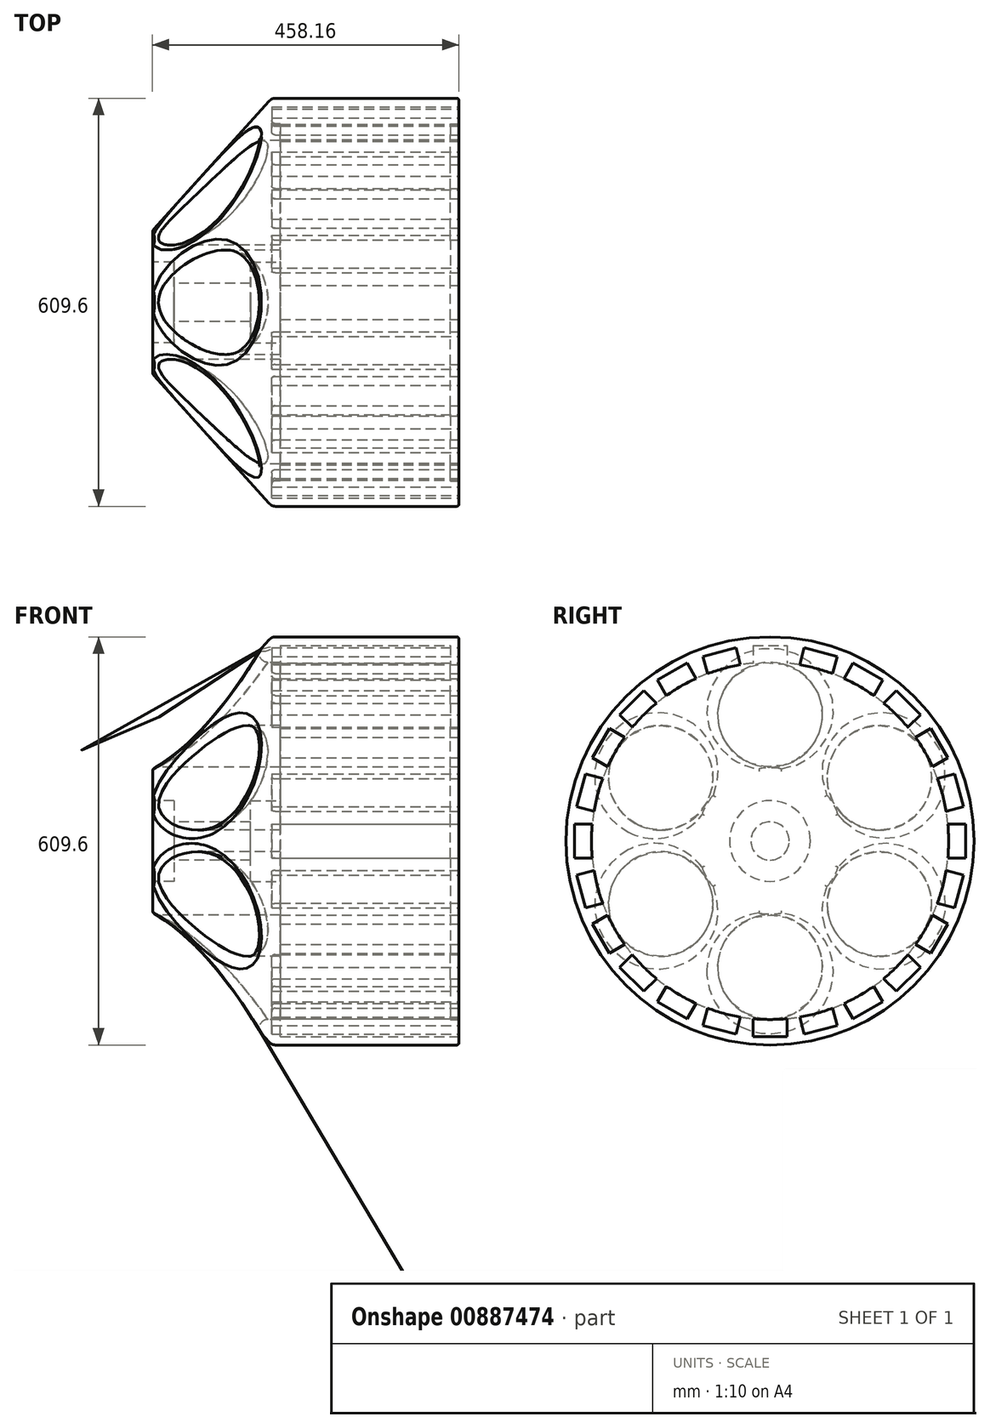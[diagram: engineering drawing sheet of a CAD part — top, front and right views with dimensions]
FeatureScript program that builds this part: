
annotation { "Feature Type Name" : "Feature", "Feature Type Description" : "" }
export const myFeature = defineFeature(function(context is Context, id is Id, definition is map)
    precondition{}
    {
        {
            var Q0;
            Q0=qCreatedBy(makeId("Front.planeOp"),FACE);
            var sketch = newSketch(context, id + "F0", { "sketchPlane" : qUnion([Q0])});
            skLineSegment(sketch, "E0", {"start": v(0, 0) * mm, "end": v(0, 304.8) * mm});
            skLineSegment(sketch, "E1", {"start": v(0, 304.8) * mm, "end": v(-279.4, 304.8) * mm});
            skLineSegment(sketch, "E2", {"start": v(-279.4, 304.8) * mm, "end": v(-457.2, 107.33) * mm});
            skLineSegment(sketch, "E3", {"start": v(-457.2, 107.33) * mm, "end": v(-457.2, 0) * mm});
            skArc(sketch, "E4", {"start": v(0, -309.7) * mm, "mid": v(-0.3, -303.83) * mm, "end": v(0, -297.95) * mm});
            skLineSegment(sketch, "E5", {"start": v(-457.2, 0) * mm, "end": v(0, 0) * mm});
            skSolve(sketch);
        }
        {
            var Q0;
            Q0=makeQuery(id+"F0.imprint","IMPRINT",FACE,{"disambiguationData":[TD([[makeQuery(id+"F0.imprint","IMPRINT",EDGE,{"derivedFrom":sQuery(id+"F0.wireOp",EDGE,"E0")}),1.0]])]});
            var Q1;
            Q1=sQuery(id+"F0.wireOp",EDGE,"E5");
            revolve(context, id + "F1", {"surfaceOperationType" : NewSurfaceOperationType.NEW, "entities" : qUnion([Q0]), "axis" : qUnion([Q1]), "revolveType" : RevolveType.FULL});
        }
        {
            var Q0;
            Q0=makeQuery(id+"F1.opRevolve","SWEPT_FACE",FACE,{"disambiguationData":[OSD([sQuery(id+"F0.wireOp",EDGE,"E0")])]});
            var sketch = newSketch(context, id + "F2", { "sketchPlane" : qUnion([Q0])});
            skCircle(sketch, "E6", {"center": v(0, 0) * mm, "radius": 266.7 * mm});
            skSolve(sketch);
        }
        {
            var Q0;
            Q0 = qSketchRegion(id + "F2", true);
            extrude(context, id + "F3", {"entities" : qUnion([Q0]), "operationType" : NewBodyOperationType.REMOVE, "oppositeDirection" : true, "depth" : 279.4 * mm, "offsetDistance" : 25.4 * mm});
        }
        {
            var Q0;
            Q0=makeQuery(id+"F1.opRevolve","SWEPT_FACE",FACE,{"disambiguationData":[OSD([sQuery(id+"F0.wireOp",EDGE,"E3")])]});
            var sketch = newSketch(context, id + "F4", { "sketchPlane" : qUnion([Q0])});
            skSolve(sketch);
        }
        {
            var Q0;
            Q0=makeQuery(id+"F4.imprint","IMPRINT",FACE,{"disambiguationData":[TD([[makeQuery(id+"F4.imprint","IMPRINT",EDGE,{"derivedFrom":makeQuery(id+"F1.opRevolve","SWEPT_EDGE",EDGE,{"disambiguationData":[OSD([sQuery(id+"F0.wireOp",EDGE,"E2"),sQuery(id+"F0.wireOp",EDGE,"E3")])]})}),1.0]])]});
            var sketch = newSketch(context, id + "F5", { "sketchPlane" : qUnion([Q0])});
            skSolve(sketch);
        }
        {
            var Q0;
            Q0=makeQuery(id+"F5.imprint","IMPRINT",FACE,{"disambiguationData":[TD([[makeQuery(id+"F5.imprint","IMPRINT",EDGE,{"derivedFrom":makeQuery(id+"F4.imprint","IMPRINT",EDGE,{"derivedFrom":makeQuery(id+"F1.opRevolve","SWEPT_EDGE",EDGE,{"disambiguationData":[OSD([sQuery(id+"F0.wireOp",EDGE,"E2"),sQuery(id+"F0.wireOp",EDGE,"E3")])]})})}),1.0]])]});
            var sketch = newSketch(context, id + "F6", { "sketchPlane" : qUnion([Q0])});
            skCircle(sketch, "E7", {"center": v(0, 0) * mm, "radius": 28.58 * mm});
            skSolve(sketch);
        }
        {
            var Q0;
            Q0 = qSketchRegion(id + "F6", true);
            extrude(context, id + "F7", {"entities" : qUnion([Q0]), "operationType" : NewBodyOperationType.REMOVE, "oppositeDirection" : true, "depth" : 298.68 * mm, "offsetDistance" : 25.4 * mm});
        }
        {
            var Q0;
            Q0=makeQuery(id+"F5.imprint","IMPRINT",FACE,{"disambiguationData":[TD([[makeQuery(id+"F5.imprint","IMPRINT",EDGE,{"derivedFrom":makeQuery(id+"F4.imprint","IMPRINT",EDGE,{"derivedFrom":makeQuery(id+"F1.opRevolve","SWEPT_EDGE",EDGE,{"disambiguationData":[OSD([sQuery(id+"F0.wireOp",EDGE,"E2"),sQuery(id+"F0.wireOp",EDGE,"E3")])]})})}),1.0]])]});
            var sketch = newSketch(context, id + "F8", { "sketchPlane" : qUnion([Q0])});
            skCircle(sketch, "E8", {"center": v(0, 0) * mm, "radius": 266.7 * mm, "construction": true});
            skCircle(sketch, "E9", {"center": v(0, 0) * mm, "radius": 101.6 * mm, "construction": true});
            skLineSegment(sketch, "E10.0", {"start": v(0, 266.7) * mm, "end": v(188.59, 188.59) * mm, "construction": true});
            skLineSegment(sketch, "E10.1", {"start": v(188.59, 188.59) * mm, "end": v(266.7, 0) * mm, "construction": true});
            skLineSegment(sketch, "E10.2", {"start": v(266.7, 0) * mm, "end": v(188.59, -188.59) * mm, "construction": true});
            skLineSegment(sketch, "E10.3", {"start": v(188.59, -188.59) * mm, "end": v(0, -266.7) * mm, "construction": true});
            skLineSegment(sketch, "E10.4", {"start": v(0, -266.7) * mm, "end": v(-188.59, -188.59) * mm, "construction": true});
            skLineSegment(sketch, "E10.5", {"start": v(-188.59, -188.59) * mm, "end": v(-266.7, 0) * mm, "construction": true});
            skLineSegment(sketch, "E10.6", {"start": v(-266.7, 0) * mm, "end": v(-188.59, 188.59) * mm, "construction": true});
            skLineSegment(sketch, "E10.7", {"start": v(-188.59, 188.59) * mm, "end": v(0, 266.7) * mm, "construction": true});
            skCircle(sketch, "E11", {"center": v(0, 188.59) * mm, "radius": 78.11 * mm});
            skCircle(sketch, "E12.1.0", {"center": v(-163.32, 94.3) * mm, "radius": 78.11 * mm});
            skCircle(sketch, "E12.2.0", {"center": v(-163.32, -94.3) * mm, "radius": 78.11 * mm});
            skCircle(sketch, "E12.3.0", {"center": v(0, -188.59) * mm, "radius": 78.11 * mm});
            skCircle(sketch, "E12.4.0", {"center": v(163.32, -94.3) * mm, "radius": 78.11 * mm});
            skCircle(sketch, "E12.5.0", {"center": v(163.32, 94.3) * mm, "radius": 78.11 * mm});
            skSolve(sketch);
        }
        {
            var Q0;
            Q0 = qSketchRegion(id + "F8", true);
            var sketch = newSketch(context, id + "F9", { "sketchPlane" : qUnion([Q0])});
            skSolve(sketch);
        }
        {
            var Q0;
            Q0 = qSketchRegion(id + "F8", true);
            var Q1;
            Q1=makeQuery(id+"F9.imprint","IMPRINT",FACE,{"disambiguationData":[TD([[makeQuery(id+"F9.imprint","IMPRINT",EDGE,{"derivedFrom":makeQuery(id+"F8.imprint","IMPRINT",EDGE,{"derivedFrom":sQuery(id+"F8.wireOp",EDGE,"E11")})}),1.0]])]});
            var Q2;
            Q2=makeQuery(id+"F9.imprint","IMPRINT",FACE,{"disambiguationData":[TD([[makeQuery(id+"F9.imprint","IMPRINT",EDGE,{"derivedFrom":makeQuery(id+"F8.imprint","IMPRINT",EDGE,{"derivedFrom":sQuery(id+"F8.wireOp",EDGE,"E12.4.0")})}),1.0]])]});
            var Q3;
            Q3=makeQuery(id+"F9.imprint","IMPRINT",FACE,{"disambiguationData":[TD([[makeQuery(id+"F9.imprint","IMPRINT",EDGE,{"derivedFrom":makeQuery(id+"F8.imprint","IMPRINT",EDGE,{"derivedFrom":sQuery(id+"F8.wireOp",EDGE,"E12.3.0")})}),1.0]])]});
            var Q4;
            Q4=makeQuery(id+"F9.imprint","IMPRINT",FACE,{"disambiguationData":[TD([[makeQuery(id+"F9.imprint","IMPRINT",EDGE,{"derivedFrom":makeQuery(id+"F8.imprint","IMPRINT",EDGE,{"derivedFrom":sQuery(id+"F8.wireOp",EDGE,"E12.2.0")})}),1.0]])]});
            var Q5;
            Q5=makeQuery(id+"F9.imprint","IMPRINT",FACE,{"disambiguationData":[TD([[makeQuery(id+"F9.imprint","IMPRINT",EDGE,{"derivedFrom":makeQuery(id+"F8.imprint","IMPRINT",EDGE,{"derivedFrom":sQuery(id+"F8.wireOp",EDGE,"E12.1.0")})}),1.0]])]});
            extrude(context, id + "F10", {"entities" : qUnion([Q0, Q1, Q2, Q3, Q4, Q5]), "operationType" : NewBodyOperationType.REMOVE, "oppositeDirection" : true, "depth" : 184.15 * mm, "offsetDistance" : 25.4 * mm});
        }
        {
            var Q0;
            Q0=makeQuery(id+"F5.imprint","IMPRINT",FACE,{"disambiguationData":[TD([[makeQuery(id+"F5.imprint","IMPRINT",EDGE,{"derivedFrom":makeQuery(id+"F4.imprint","IMPRINT",EDGE,{"derivedFrom":makeQuery(id+"F1.opRevolve","SWEPT_EDGE",EDGE,{"disambiguationData":[OSD([sQuery(id+"F0.wireOp",EDGE,"E2"),sQuery(id+"F0.wireOp",EDGE,"E3")])]})})}),1.0]])]});
            var sketch = newSketch(context, id + "F11", { "sketchPlane" : qUnion([Q0])});
            skCircle(sketch, "E13", {"center": v(0, 0) * mm, "radius": 60.33 * mm});
            skSolve(sketch);
        }
        {
            var Q0;
            Q0 = qSketchRegion(id + "F11", true);
            extrude(context, id + "F12", {"entities" : qUnion([Q0]), "operationType" : NewBodyOperationType.REMOVE, "oppositeDirection" : true, "depth" : 31.75 * mm, "offsetDistance" : 25.4 * mm});
        }
        {
            var Q0;
            Q0=makeQuery(id+"F3.boolean.opBoolean","COPY",FACE,{"derivedFrom":makeQuery(id+"F3.opExtrude","CAP_FACE",FACE,{"disambiguationData":[OSD([sQuery(id+"F2.wireOp",EDGE,"E6")])],"isStart":false})});
            var sketch = newSketch(context, id + "F13", { "sketchPlane" : qUnion([Q0])});
            skCircle(sketch, "E14", {"center": v(0, 0) * mm, "radius": 60.33 * mm});
            skSolve(sketch);
        }
        {
            var Q0;
            Q0 = qSketchRegion(id + "F13", true);
            var Q1;
            Q1=makeQuery(id+"F13.imprint","IMPRINT",FACE,{"disambiguationData":[TD([[makeQuery(id+"F13.imprint","IMPRINT",EDGE,{"derivedFrom":sQuery(id+"F13.wireOp",EDGE,"E14")}),1.0]])]});
            extrude(context, id + "F14", {"entities" : qUnion([Q0, Q1]), "operationType" : NewBodyOperationType.REMOVE, "oppositeDirection" : true, "depth" : 31.75 * mm, "offsetDistance" : 25.4 * mm});
        }
        {
            var Q0;
            Q0=makeQuery(id+"F1.opRevolve","SWEPT_FACE",FACE,{"disambiguationData":[OSD([sQuery(id+"F0.wireOp",EDGE,"E0")])]});
            var sketch = newSketch(context, id + "F15", { "sketchPlane" : qUnion([Q0])});
            skLineSegment(sketch, "E15", {"start": v(0, 292.1) * mm, "end": v(0, 266.7) * mm, "construction": true});
            skLineSegment(sketch, "E16", {"start": v(0, 292.1) * mm, "end": v(25.4, 292.1) * mm});
            skLineSegment(sketch, "E17", {"start": v(25.4, 292.1) * mm, "end": v(25.4, 265.49) * mm});
            skLineSegment(sketch, "E18.MirrorCS", {"start": v(0, 292.1) * mm, "end": v(-25.4, 292.1) * mm});
            skLineSegment(sketch, "E19.MirrorCS", {"start": v(-25.4, 292.1) * mm, "end": v(-25.4, 265.49) * mm});
            skLineSegment(sketch, "E20.1.0", {"start": v(-51.07, 288.72) * mm, "end": v(-44.18, 263.02) * mm});
            skLineSegment(sketch, "E20.1.1", {"start": v(-75.6, 282.15) * mm, "end": v(-51.07, 288.72) * mm});
            skLineSegment(sketch, "E20.1.2", {"start": v(-75.6, 282.15) * mm, "end": v(-100.14, 275.57) * mm});
            skLineSegment(sketch, "E20.1.3", {"start": v(-100.14, 275.57) * mm, "end": v(-93.25, 249.87) * mm});
            skLineSegment(sketch, "E20.2.0", {"start": v(-124.05, 265.67) * mm, "end": v(-110.75, 242.62) * mm});
            skLineSegment(sketch, "E20.2.1", {"start": v(-146.05, 252.97) * mm, "end": v(-124.05, 265.67) * mm});
            skLineSegment(sketch, "E20.2.2", {"start": v(-146.05, 252.97) * mm, "end": v(-168.05, 240.27) * mm});
            skLineSegment(sketch, "E20.2.3", {"start": v(-168.05, 240.27) * mm, "end": v(-154.74, 217.22) * mm});
            skLineSegment(sketch, "E20.3.0", {"start": v(-188.59, 224.5) * mm, "end": v(-169.77, 205.69) * mm});
            skLineSegment(sketch, "E20.3.1", {"start": v(-206.55, 206.55) * mm, "end": v(-188.59, 224.5) * mm});
            skLineSegment(sketch, "E20.3.2", {"start": v(-206.55, 206.55) * mm, "end": v(-224.5, 188.59) * mm});
            skLineSegment(sketch, "E20.3.3", {"start": v(-224.5, 188.59) * mm, "end": v(-205.69, 169.77) * mm});
            skLineSegment(sketch, "E20.4.0", {"start": v(-240.27, 168.05) * mm, "end": v(-217.22, 154.74) * mm});
            skLineSegment(sketch, "E20.4.1", {"start": v(-252.97, 146.05) * mm, "end": v(-240.27, 168.05) * mm});
            skLineSegment(sketch, "E20.4.2", {"start": v(-252.97, 146.05) * mm, "end": v(-265.67, 124.05) * mm});
            skLineSegment(sketch, "E20.4.3", {"start": v(-265.67, 124.05) * mm, "end": v(-242.62, 110.75) * mm});
            skLineSegment(sketch, "E20.5.0", {"start": v(-275.57, 100.14) * mm, "end": v(-249.87, 93.25) * mm});
            skLineSegment(sketch, "E20.5.1", {"start": v(-282.15, 75.6) * mm, "end": v(-275.57, 100.14) * mm});
            skLineSegment(sketch, "E20.5.2", {"start": v(-282.15, 75.6) * mm, "end": v(-288.72, 51.07) * mm});
            skLineSegment(sketch, "E20.5.3", {"start": v(-288.72, 51.07) * mm, "end": v(-263.02, 44.18) * mm});
            skLineSegment(sketch, "E20.6.0", {"start": v(-292.1, 25.4) * mm, "end": v(-265.49, 25.4) * mm});
            skLineSegment(sketch, "E20.6.1", {"start": v(-292.1, 0) * mm, "end": v(-292.1, 25.4) * mm});
            skLineSegment(sketch, "E20.6.2", {"start": v(-292.1, 0) * mm, "end": v(-292.1, -25.4) * mm});
            skLineSegment(sketch, "E20.6.3", {"start": v(-292.1, -25.4) * mm, "end": v(-265.49, -25.4) * mm});
            skLineSegment(sketch, "E20.7.0", {"start": v(-288.72, -51.07) * mm, "end": v(-263.02, -44.18) * mm});
            skLineSegment(sketch, "E20.7.1", {"start": v(-282.15, -75.6) * mm, "end": v(-288.72, -51.07) * mm});
            skLineSegment(sketch, "E20.7.2", {"start": v(-282.15, -75.6) * mm, "end": v(-275.57, -100.14) * mm});
            skLineSegment(sketch, "E20.7.3", {"start": v(-275.57, -100.14) * mm, "end": v(-249.87, -93.25) * mm});
            skLineSegment(sketch, "E20.8.0", {"start": v(-265.67, -124.05) * mm, "end": v(-242.62, -110.75) * mm});
            skLineSegment(sketch, "E20.8.1", {"start": v(-252.97, -146.05) * mm, "end": v(-265.67, -124.05) * mm});
            skLineSegment(sketch, "E20.8.2", {"start": v(-252.97, -146.05) * mm, "end": v(-240.27, -168.05) * mm});
            skLineSegment(sketch, "E20.8.3", {"start": v(-240.27, -168.05) * mm, "end": v(-217.22, -154.74) * mm});
            skLineSegment(sketch, "E20.9.0", {"start": v(-224.5, -188.59) * mm, "end": v(-205.69, -169.77) * mm});
            skLineSegment(sketch, "E20.9.1", {"start": v(-206.55, -206.55) * mm, "end": v(-224.5, -188.59) * mm});
            skLineSegment(sketch, "E20.9.2", {"start": v(-206.55, -206.55) * mm, "end": v(-188.59, -224.5) * mm});
            skLineSegment(sketch, "E20.9.3", {"start": v(-188.59, -224.5) * mm, "end": v(-169.77, -205.69) * mm});
            skLineSegment(sketch, "E20.10.0", {"start": v(-168.05, -240.27) * mm, "end": v(-154.74, -217.22) * mm});
            skLineSegment(sketch, "E20.10.1", {"start": v(-146.05, -252.97) * mm, "end": v(-168.05, -240.27) * mm});
            skLineSegment(sketch, "E20.10.2", {"start": v(-146.05, -252.97) * mm, "end": v(-124.05, -265.67) * mm});
            skLineSegment(sketch, "E20.10.3", {"start": v(-124.05, -265.67) * mm, "end": v(-110.75, -242.62) * mm});
            skLineSegment(sketch, "E20.11.0", {"start": v(-100.14, -275.57) * mm, "end": v(-93.25, -249.87) * mm});
            skLineSegment(sketch, "E20.11.1", {"start": v(-75.6, -282.15) * mm, "end": v(-100.14, -275.57) * mm});
            skLineSegment(sketch, "E20.11.2", {"start": v(-75.6, -282.15) * mm, "end": v(-51.07, -288.72) * mm});
            skLineSegment(sketch, "E20.11.3", {"start": v(-51.07, -288.72) * mm, "end": v(-44.18, -263.02) * mm});
            skLineSegment(sketch, "E20.12.0", {"start": v(-25.4, -292.1) * mm, "end": v(-25.4, -265.49) * mm});
            skLineSegment(sketch, "E20.12.1", {"start": v(0, -292.1) * mm, "end": v(-25.4, -292.1) * mm});
            skLineSegment(sketch, "E20.12.2", {"start": v(0, -292.1) * mm, "end": v(25.4, -292.1) * mm});
            skLineSegment(sketch, "E20.12.3", {"start": v(25.4, -292.1) * mm, "end": v(25.4, -265.49) * mm});
            skLineSegment(sketch, "E20.13.0", {"start": v(51.07, -288.72) * mm, "end": v(44.18, -263.02) * mm});
            skLineSegment(sketch, "E20.13.1", {"start": v(75.6, -282.15) * mm, "end": v(51.07, -288.72) * mm});
            skLineSegment(sketch, "E20.13.2", {"start": v(75.6, -282.15) * mm, "end": v(100.14, -275.57) * mm});
            skLineSegment(sketch, "E20.13.3", {"start": v(100.14, -275.57) * mm, "end": v(93.25, -249.87) * mm});
            skLineSegment(sketch, "E20.14.0", {"start": v(124.05, -265.67) * mm, "end": v(110.75, -242.62) * mm});
            skLineSegment(sketch, "E20.14.1", {"start": v(146.05, -252.97) * mm, "end": v(124.05, -265.67) * mm});
            skLineSegment(sketch, "E20.14.2", {"start": v(146.05, -252.97) * mm, "end": v(168.05, -240.27) * mm});
            skLineSegment(sketch, "E20.14.3", {"start": v(168.05, -240.27) * mm, "end": v(154.74, -217.22) * mm});
            skLineSegment(sketch, "E20.15.0", {"start": v(188.59, -224.5) * mm, "end": v(169.77, -205.69) * mm});
            skLineSegment(sketch, "E20.15.1", {"start": v(206.55, -206.55) * mm, "end": v(188.59, -224.5) * mm});
            skLineSegment(sketch, "E20.15.2", {"start": v(206.55, -206.55) * mm, "end": v(224.5, -188.59) * mm});
            skLineSegment(sketch, "E20.15.3", {"start": v(224.5, -188.59) * mm, "end": v(205.69, -169.77) * mm});
            skLineSegment(sketch, "E20.16.0", {"start": v(240.27, -168.05) * mm, "end": v(217.22, -154.74) * mm});
            skLineSegment(sketch, "E20.16.1", {"start": v(252.97, -146.05) * mm, "end": v(240.27, -168.05) * mm});
            skLineSegment(sketch, "E20.16.2", {"start": v(252.97, -146.05) * mm, "end": v(265.67, -124.05) * mm});
            skLineSegment(sketch, "E20.16.3", {"start": v(265.67, -124.05) * mm, "end": v(242.62, -110.75) * mm});
            skLineSegment(sketch, "E20.17.0", {"start": v(275.57, -100.14) * mm, "end": v(249.87, -93.25) * mm});
            skLineSegment(sketch, "E20.17.1", {"start": v(282.15, -75.6) * mm, "end": v(275.57, -100.14) * mm});
            skLineSegment(sketch, "E20.17.2", {"start": v(282.15, -75.6) * mm, "end": v(288.72, -51.07) * mm});
            skLineSegment(sketch, "E20.17.3", {"start": v(288.72, -51.07) * mm, "end": v(263.02, -44.18) * mm});
            skLineSegment(sketch, "E20.18.0", {"start": v(292.1, -25.4) * mm, "end": v(265.49, -25.4) * mm});
            skLineSegment(sketch, "E20.18.1", {"start": v(292.1, 0) * mm, "end": v(292.1, -25.4) * mm});
            skLineSegment(sketch, "E20.18.2", {"start": v(292.1, 0) * mm, "end": v(292.1, 25.4) * mm});
            skLineSegment(sketch, "E20.18.3", {"start": v(292.1, 25.4) * mm, "end": v(265.49, 25.4) * mm});
            skLineSegment(sketch, "E20.19.0", {"start": v(288.72, 51.07) * mm, "end": v(263.02, 44.18) * mm});
            skLineSegment(sketch, "E20.19.1", {"start": v(282.15, 75.6) * mm, "end": v(288.72, 51.07) * mm});
            skLineSegment(sketch, "E20.19.2", {"start": v(282.15, 75.6) * mm, "end": v(275.57, 100.14) * mm});
            skLineSegment(sketch, "E20.19.3", {"start": v(275.57, 100.14) * mm, "end": v(249.87, 93.25) * mm});
            skLineSegment(sketch, "E20.20.0", {"start": v(265.67, 124.05) * mm, "end": v(242.62, 110.75) * mm});
            skLineSegment(sketch, "E20.20.1", {"start": v(252.97, 146.05) * mm, "end": v(265.67, 124.05) * mm});
            skLineSegment(sketch, "E20.20.2", {"start": v(252.97, 146.05) * mm, "end": v(240.27, 168.05) * mm});
            skLineSegment(sketch, "E20.20.3", {"start": v(240.27, 168.05) * mm, "end": v(217.22, 154.74) * mm});
            skLineSegment(sketch, "E20.21.0", {"start": v(224.5, 188.59) * mm, "end": v(205.69, 169.77) * mm});
            skLineSegment(sketch, "E20.21.1", {"start": v(206.55, 206.55) * mm, "end": v(224.5, 188.59) * mm});
            skLineSegment(sketch, "E20.21.2", {"start": v(206.55, 206.55) * mm, "end": v(188.59, 224.5) * mm});
            skLineSegment(sketch, "E20.21.3", {"start": v(188.59, 224.5) * mm, "end": v(169.77, 205.69) * mm});
            skLineSegment(sketch, "E20.22.0", {"start": v(168.05, 240.27) * mm, "end": v(154.74, 217.22) * mm});
            skLineSegment(sketch, "E20.22.1", {"start": v(146.05, 252.97) * mm, "end": v(168.05, 240.27) * mm});
            skLineSegment(sketch, "E20.22.2", {"start": v(146.05, 252.97) * mm, "end": v(124.05, 265.67) * mm});
            skLineSegment(sketch, "E20.22.3", {"start": v(124.05, 265.67) * mm, "end": v(110.75, 242.62) * mm});
            skLineSegment(sketch, "E20.23.0", {"start": v(100.14, 275.57) * mm, "end": v(93.25, 249.87) * mm});
            skLineSegment(sketch, "E20.23.1", {"start": v(75.6, 282.15) * mm, "end": v(100.14, 275.57) * mm});
            skLineSegment(sketch, "E20.23.2", {"start": v(75.6, 282.15) * mm, "end": v(51.07, 288.72) * mm});
            skLineSegment(sketch, "E20.23.3", {"start": v(51.07, 288.72) * mm, "end": v(44.18, 263.02) * mm});
            skPoint(sketch, "E20.center", {"position": v(0, 0) * mm});
            skSolve(sketch);
        }
        {
            var Q0;
            Q0=makeQuery(id+"F15.imprint","IMPRINT",FACE,{"disambiguationData":[TD([[makeQuery(id+"F15.imprint","IMPRINT",EDGE,{"derivedFrom":sQuery(id+"F15.wireOp",EDGE,"E16")}),-1.0]])]});
            var Q1;
            {var subQ1=sQuery(id+"F15.wireOp",EDGE,"E20.23.0");Q1=makeQuery(id+"F15.imprint","IMPRINT",FACE,{"disambiguationData":[TD([[makeQuery(id+"F15.imprint","IMPRINT",EDGE,{"derivedFrom":subQ1}),-1.0]])]});}
            var Q2;
            {var subQ1=sQuery(id+"F15.wireOp",EDGE,"E20.22.0");Q2=makeQuery(id+"F15.imprint","IMPRINT",FACE,{"disambiguationData":[TD([[makeQuery(id+"F15.imprint","IMPRINT",EDGE,{"derivedFrom":subQ1}),-1.0]])]});}
            var Q3;
            {var subQ1=sQuery(id+"F15.wireOp",EDGE,"E20.21.0");Q3=makeQuery(id+"F15.imprint","IMPRINT",FACE,{"disambiguationData":[TD([[makeQuery(id+"F15.imprint","IMPRINT",EDGE,{"derivedFrom":subQ1}),-1.0]])]});}
            var Q4;
            {var subQ1=sQuery(id+"F15.wireOp",EDGE,"E20.20.0");Q4=makeQuery(id+"F15.imprint","IMPRINT",FACE,{"disambiguationData":[TD([[makeQuery(id+"F15.imprint","IMPRINT",EDGE,{"derivedFrom":subQ1}),-1.0]])]});}
            var Q5;
            {var subQ1=sQuery(id+"F15.wireOp",EDGE,"E20.19.0");Q5=makeQuery(id+"F15.imprint","IMPRINT",FACE,{"disambiguationData":[TD([[makeQuery(id+"F15.imprint","IMPRINT",EDGE,{"derivedFrom":subQ1}),-1.0]])]});}
            var Q6;
            {var subQ1=sQuery(id+"F15.wireOp",EDGE,"E20.17.0");Q6=makeQuery(id+"F15.imprint","IMPRINT",FACE,{"disambiguationData":[TD([[makeQuery(id+"F15.imprint","IMPRINT",EDGE,{"derivedFrom":subQ1}),-1.0]])]});}
            var Q7;
            {var subQ1=sQuery(id+"F15.wireOp",EDGE,"E20.16.0");Q7=makeQuery(id+"F15.imprint","IMPRINT",FACE,{"disambiguationData":[TD([[makeQuery(id+"F15.imprint","IMPRINT",EDGE,{"derivedFrom":subQ1}),-1.0]])]});}
            var Q8;
            {var subQ1=sQuery(id+"F15.wireOp",EDGE,"E20.15.0");Q8=makeQuery(id+"F15.imprint","IMPRINT",FACE,{"disambiguationData":[TD([[makeQuery(id+"F15.imprint","IMPRINT",EDGE,{"derivedFrom":subQ1}),-1.0]])]});}
            var Q9;
            {var subQ1=sQuery(id+"F15.wireOp",EDGE,"E20.14.0");Q9=makeQuery(id+"F15.imprint","IMPRINT",FACE,{"disambiguationData":[TD([[makeQuery(id+"F15.imprint","IMPRINT",EDGE,{"derivedFrom":subQ1}),-1.0]])]});}
            var Q10;
            {var subQ1=sQuery(id+"F15.wireOp",EDGE,"E20.13.0");Q10=makeQuery(id+"F15.imprint","IMPRINT",FACE,{"disambiguationData":[TD([[makeQuery(id+"F15.imprint","IMPRINT",EDGE,{"derivedFrom":subQ1}),-1.0]])]});}
            var Q11;
            {var subQ1=sQuery(id+"F15.wireOp",EDGE,"E20.12.0");Q11=makeQuery(id+"F15.imprint","IMPRINT",FACE,{"disambiguationData":[TD([[makeQuery(id+"F15.imprint","IMPRINT",EDGE,{"derivedFrom":subQ1}),-1.0]])]});}
            var Q12;
            {var subQ1=sQuery(id+"F15.wireOp",EDGE,"E20.11.0");Q12=makeQuery(id+"F15.imprint","IMPRINT",FACE,{"disambiguationData":[TD([[makeQuery(id+"F15.imprint","IMPRINT",EDGE,{"derivedFrom":subQ1}),-1.0]])]});}
            var Q13;
            {var subQ1=sQuery(id+"F15.wireOp",EDGE,"E20.10.0");Q13=makeQuery(id+"F15.imprint","IMPRINT",FACE,{"disambiguationData":[TD([[makeQuery(id+"F15.imprint","IMPRINT",EDGE,{"derivedFrom":subQ1}),-1.0]])]});}
            var Q14;
            {var subQ1=sQuery(id+"F15.wireOp",EDGE,"E20.8.0");Q14=makeQuery(id+"F15.imprint","IMPRINT",FACE,{"disambiguationData":[TD([[makeQuery(id+"F15.imprint","IMPRINT",EDGE,{"derivedFrom":subQ1}),-1.0]])]});}
            var Q15;
            {var subQ1=sQuery(id+"F15.wireOp",EDGE,"E20.7.0");Q15=makeQuery(id+"F15.imprint","IMPRINT",FACE,{"disambiguationData":[TD([[makeQuery(id+"F15.imprint","IMPRINT",EDGE,{"derivedFrom":subQ1}),-1.0]])]});}
            var Q16;
            {var subQ1=sQuery(id+"F15.wireOp",EDGE,"E20.9.0");Q16=makeQuery(id+"F15.imprint","IMPRINT",FACE,{"disambiguationData":[TD([[makeQuery(id+"F15.imprint","IMPRINT",EDGE,{"derivedFrom":subQ1}),-1.0]])]});}
            var Q17;
            {var subQ1=sQuery(id+"F15.wireOp",EDGE,"E20.6.0");Q17=makeQuery(id+"F15.imprint","IMPRINT",FACE,{"disambiguationData":[TD([[makeQuery(id+"F15.imprint","IMPRINT",EDGE,{"derivedFrom":subQ1}),-1.0]])]});}
            var Q18;
            {var subQ1=sQuery(id+"F15.wireOp",EDGE,"E20.5.0");Q18=makeQuery(id+"F15.imprint","IMPRINT",FACE,{"disambiguationData":[TD([[makeQuery(id+"F15.imprint","IMPRINT",EDGE,{"derivedFrom":subQ1}),-1.0]])]});}
            var Q19;
            {var subQ1=sQuery(id+"F15.wireOp",EDGE,"E20.4.0");Q19=makeQuery(id+"F15.imprint","IMPRINT",FACE,{"disambiguationData":[TD([[makeQuery(id+"F15.imprint","IMPRINT",EDGE,{"derivedFrom":subQ1}),-1.0]])]});}
            var Q20;
            {var subQ1=sQuery(id+"F15.wireOp",EDGE,"E20.2.0");Q20=makeQuery(id+"F15.imprint","IMPRINT",FACE,{"disambiguationData":[TD([[makeQuery(id+"F15.imprint","IMPRINT",EDGE,{"derivedFrom":subQ1}),-1.0]])]});}
            var Q21;
            {var subQ1=sQuery(id+"F15.wireOp",EDGE,"E20.1.0");Q21=makeQuery(id+"F15.imprint","IMPRINT",FACE,{"disambiguationData":[TD([[makeQuery(id+"F15.imprint","IMPRINT",EDGE,{"derivedFrom":subQ1}),-1.0]])]});}
            var Q22;
            {var subQ1=sQuery(id+"F15.wireOp",EDGE,"E20.3.0");Q22=makeQuery(id+"F15.imprint","IMPRINT",FACE,{"disambiguationData":[TD([[makeQuery(id+"F15.imprint","IMPRINT",EDGE,{"derivedFrom":subQ1}),-1.0]])]});}
            var Q23;
            {var subQ1=sQuery(id+"F15.wireOp",EDGE,"E20.18.0");Q23=makeQuery(id+"F15.imprint","IMPRINT",FACE,{"disambiguationData":[TD([[makeQuery(id+"F15.imprint","IMPRINT",EDGE,{"derivedFrom":subQ1}),-1.0]])]});}
            extrude(context, id + "F16", {"entities" : qUnion([Q0, Q1, Q2, Q3, Q4, Q5, Q6, Q7, Q8, Q9, Q10, Q11, Q12, Q13, Q14, Q15, Q16, Q17, Q18, Q19, Q20, Q21, Q22, Q23]), "operationType" : NewBodyOperationType.REMOVE, "oppositeDirection" : true, "depth" : 279.4 * mm, "offsetDistance" : 25.4 * mm});
        }
        {
            var Q0;
            {var subQ0=sQuery(id+"F8.wireOp",EDGE,"E12.2.0");Q0=makeQuery(id+"F10.boolean.opBoolean","INTERSECT",EDGE,{"derivedFrom":[makeQuery(id+"F1.opRevolve","SWEPT_FACE",FACE,{"disambiguationData":[OSD([sQuery(id+"F0.wireOp",EDGE,"E2")])]}),makeQuery(id+"F10.opExtrude","SWEPT_FACE",FACE,{"disambiguationData":[OSD([subQ0]),TDD([makeQuery(id+"F8.imprint","IMPRINT",EDGE,{"derivedFrom":subQ0})])]})]});}
            var Q1;
            {var subQ0=sQuery(id+"F8.wireOp",EDGE,"E12.1.0");Q1=makeQuery(id+"F10.boolean.opBoolean","INTERSECT",EDGE,{"derivedFrom":[makeQuery(id+"F1.opRevolve","SWEPT_FACE",FACE,{"disambiguationData":[OSD([sQuery(id+"F0.wireOp",EDGE,"E2")])]}),makeQuery(id+"F10.opExtrude","SWEPT_FACE",FACE,{"disambiguationData":[OSD([subQ0]),TDD([makeQuery(id+"F8.imprint","IMPRINT",EDGE,{"derivedFrom":subQ0})])]})]});}
            var Q2;
            {var subQ0=sQuery(id+"F8.wireOp",EDGE,"E11");Q2=makeQuery(id+"F10.boolean.opBoolean","INTERSECT",EDGE,{"derivedFrom":[makeQuery(id+"F1.opRevolve","SWEPT_FACE",FACE,{"disambiguationData":[OSD([sQuery(id+"F0.wireOp",EDGE,"E2")])]}),makeQuery(id+"F10.opExtrude","SWEPT_FACE",FACE,{"disambiguationData":[OSD([subQ0]),TDD([makeQuery(id+"F8.imprint","IMPRINT",EDGE,{"derivedFrom":subQ0})])]})]});}
            var Q3;
            Q3=makeQuery(id+"F10.boolean.opBoolean","INTERSECT",EDGE,{"derivedFrom":[makeQuery(id+"F1.opRevolve","SWEPT_FACE",FACE,{"disambiguationData":[OSD([sQuery(id+"F0.wireOp",EDGE,"E2")])]}),makeQuery(id+"F10.opExtrude","SWEPT_FACE",FACE,{"disambiguationData":[OSD([sQuery(id+"F8.wireOp",EDGE,"E12.5.0")])]})]});
            var Q4;
            {var subQ0=sQuery(id+"F8.wireOp",EDGE,"E12.4.0");Q4=makeQuery(id+"F10.boolean.opBoolean","INTERSECT",EDGE,{"derivedFrom":[makeQuery(id+"F1.opRevolve","SWEPT_FACE",FACE,{"disambiguationData":[OSD([sQuery(id+"F0.wireOp",EDGE,"E2")])]}),makeQuery(id+"F10.opExtrude","SWEPT_FACE",FACE,{"disambiguationData":[OSD([subQ0]),TDD([makeQuery(id+"F8.imprint","IMPRINT",EDGE,{"derivedFrom":subQ0})])]})]});}
            var Q5;
            {var subQ0=sQuery(id+"F8.wireOp",EDGE,"E12.3.0");Q5=makeQuery(id+"F10.boolean.opBoolean","INTERSECT",EDGE,{"derivedFrom":[makeQuery(id+"F1.opRevolve","SWEPT_FACE",FACE,{"disambiguationData":[OSD([sQuery(id+"F0.wireOp",EDGE,"E2")])]}),makeQuery(id+"F10.opExtrude","SWEPT_FACE",FACE,{"disambiguationData":[OSD([subQ0]),TDD([makeQuery(id+"F8.imprint","IMPRINT",EDGE,{"derivedFrom":subQ0})])]})]});}
            var Q6;
            Q6=makeQuery(id+"F1.opRevolve","SWEPT_EDGE",EDGE,{"disambiguationData":[OSD([sQuery(id+"F0.wireOp",EDGE,"E1"),sQuery(id+"F0.wireOp",EDGE,"E2")])]});
            fillet(context, id + "F17", {"entities" : qUnion([Q0, Q1, Q2, Q3, Q4, Q5, Q6]), "radius" : 12.7 * mm, "tangentPropagation" : true, "allowEdgeOverflow" : false});
        }
        {
            var Q0;
            Q0=makeQuery(id+"F1.opRevolve","SWEPT_EDGE",EDGE,{"disambiguationData":[OSD([sQuery(id+"F0.wireOp",EDGE,"E2"),sQuery(id+"F0.wireOp",EDGE,"E3")])]});
            fillet(context, id + "F18", {"entities" : qUnion([Q0]), "radius" : 5.08 * mm, "tangentPropagation" : true, "allowEdgeOverflow" : false});
        }
        {
            var Q0;
            Q0=makeQuery(id+"F1.opRevolve","SWEPT_EDGE",EDGE,{"disambiguationData":[OSD([sQuery(id+"F0.wireOp",EDGE,"E0"),sQuery(id+"F0.wireOp",EDGE,"E1")])]});
            fillet(context, id + "F19", {"entities" : qUnion([Q0]), "radius" : 3.17 * mm, "tangentPropagation" : true, "allowEdgeOverflow" : false});
        }
        {
            var Q0;
            {var subQ0=sQuery(id+"F2.wireOp",EDGE,"E6");Q0=makeQuery(id+"F16.boolean.opBoolean","MERGE",FACE,{"derivedFrom":[makeQuery(id+"F3.boolean.opBoolean","COPY",FACE,{"derivedFrom":makeQuery(id+"F3.opExtrude","CAP_FACE",FACE,{"disambiguationData":[OSD([subQ0])],"isStart":false})})],"fromTools":[makeQuery(id+"F16.opExtrude","CAP_FACE",FACE,{"disambiguationData":[OSD([subQ0,sQuery(id+"F15.wireOp",EDGE,"E16"),sQuery(id+"F15.wireOp",EDGE,"E17"),sQuery(id+"F15.wireOp",EDGE,"E18.MirrorCS"),sQuery(id+"F15.wireOp",EDGE,"E19.MirrorCS")])],"isStart":false}),makeQuery(id+"F16.opExtrude","CAP_FACE",FACE,{"disambiguationData":[OSD([subQ0,sQuery(id+"F15.wireOp",EDGE,"E20.1.0"),sQuery(id+"F15.wireOp",EDGE,"E20.1.1"),sQuery(id+"F15.wireOp",EDGE,"E20.1.2"),sQuery(id+"F15.wireOp",EDGE,"E20.1.3")])],"isStart":false}),makeQuery(id+"F16.opExtrude","CAP_FACE",FACE,{"disambiguationData":[OSD([subQ0,sQuery(id+"F15.wireOp",EDGE,"E20.2.0"),sQuery(id+"F15.wireOp",EDGE,"E20.2.1"),sQuery(id+"F15.wireOp",EDGE,"E20.2.2"),sQuery(id+"F15.wireOp",EDGE,"E20.2.3")])],"isStart":false}),makeQuery(id+"F16.opExtrude","CAP_FACE",FACE,{"disambiguationData":[OSD([subQ0,sQuery(id+"F15.wireOp",EDGE,"E20.3.0"),sQuery(id+"F15.wireOp",EDGE,"E20.3.1"),sQuery(id+"F15.wireOp",EDGE,"E20.3.2"),sQuery(id+"F15.wireOp",EDGE,"E20.3.3")])],"isStart":false}),makeQuery(id+"F16.opExtrude","CAP_FACE",FACE,{"disambiguationData":[OSD([subQ0,sQuery(id+"F15.wireOp",EDGE,"E20.4.0"),sQuery(id+"F15.wireOp",EDGE,"E20.4.1"),sQuery(id+"F15.wireOp",EDGE,"E20.4.2"),sQuery(id+"F15.wireOp",EDGE,"E20.4.3")])],"isStart":false}),makeQuery(id+"F16.opExtrude","CAP_FACE",FACE,{"disambiguationData":[OSD([subQ0,sQuery(id+"F15.wireOp",EDGE,"E20.5.0"),sQuery(id+"F15.wireOp",EDGE,"E20.5.1"),sQuery(id+"F15.wireOp",EDGE,"E20.5.2"),sQuery(id+"F15.wireOp",EDGE,"E20.5.3")])],"isStart":false}),makeQuery(id+"F16.opExtrude","CAP_FACE",FACE,{"disambiguationData":[OSD([subQ0,sQuery(id+"F15.wireOp",EDGE,"E20.6.0"),sQuery(id+"F15.wireOp",EDGE,"E20.6.1"),sQuery(id+"F15.wireOp",EDGE,"E20.6.2"),sQuery(id+"F15.wireOp",EDGE,"E20.6.3")])],"isStart":false}),makeQuery(id+"F16.opExtrude","CAP_FACE",FACE,{"disambiguationData":[OSD([subQ0,sQuery(id+"F15.wireOp",EDGE,"E20.7.0"),sQuery(id+"F15.wireOp",EDGE,"E20.7.1"),sQuery(id+"F15.wireOp",EDGE,"E20.7.2"),sQuery(id+"F15.wireOp",EDGE,"E20.7.3")])],"isStart":false}),makeQuery(id+"F16.opExtrude","CAP_FACE",FACE,{"disambiguationData":[OSD([subQ0,sQuery(id+"F15.wireOp",EDGE,"E20.8.0"),sQuery(id+"F15.wireOp",EDGE,"E20.8.1"),sQuery(id+"F15.wireOp",EDGE,"E20.8.2"),sQuery(id+"F15.wireOp",EDGE,"E20.8.3")])],"isStart":false}),makeQuery(id+"F16.opExtrude","CAP_FACE",FACE,{"disambiguationData":[OSD([subQ0,sQuery(id+"F15.wireOp",EDGE,"E20.9.0"),sQuery(id+"F15.wireOp",EDGE,"E20.9.1"),sQuery(id+"F15.wireOp",EDGE,"E20.9.2"),sQuery(id+"F15.wireOp",EDGE,"E20.9.3")])],"isStart":false}),makeQuery(id+"F16.opExtrude","CAP_FACE",FACE,{"disambiguationData":[OSD([subQ0,sQuery(id+"F15.wireOp",EDGE,"E20.10.0"),sQuery(id+"F15.wireOp",EDGE,"E20.10.1"),sQuery(id+"F15.wireOp",EDGE,"E20.10.2"),sQuery(id+"F15.wireOp",EDGE,"E20.10.3")])],"isStart":false}),makeQuery(id+"F16.opExtrude","CAP_FACE",FACE,{"disambiguationData":[OSD([subQ0,sQuery(id+"F15.wireOp",EDGE,"E20.11.0"),sQuery(id+"F15.wireOp",EDGE,"E20.11.1"),sQuery(id+"F15.wireOp",EDGE,"E20.11.2"),sQuery(id+"F15.wireOp",EDGE,"E20.11.3")])],"isStart":false}),makeQuery(id+"F16.opExtrude","CAP_FACE",FACE,{"disambiguationData":[OSD([subQ0,sQuery(id+"F15.wireOp",EDGE,"E20.12.0"),sQuery(id+"F15.wireOp",EDGE,"E20.12.1"),sQuery(id+"F15.wireOp",EDGE,"E20.12.2"),sQuery(id+"F15.wireOp",EDGE,"E20.12.3")])],"isStart":false}),makeQuery(id+"F16.opExtrude","CAP_FACE",FACE,{"disambiguationData":[OSD([subQ0,sQuery(id+"F15.wireOp",EDGE,"E20.13.0"),sQuery(id+"F15.wireOp",EDGE,"E20.13.1"),sQuery(id+"F15.wireOp",EDGE,"E20.13.2"),sQuery(id+"F15.wireOp",EDGE,"E20.13.3")])],"isStart":false}),makeQuery(id+"F16.opExtrude","CAP_FACE",FACE,{"disambiguationData":[OSD([subQ0,sQuery(id+"F15.wireOp",EDGE,"E20.14.0"),sQuery(id+"F15.wireOp",EDGE,"E20.14.1"),sQuery(id+"F15.wireOp",EDGE,"E20.14.2"),sQuery(id+"F15.wireOp",EDGE,"E20.14.3")])],"isStart":false}),makeQuery(id+"F16.opExtrude","CAP_FACE",FACE,{"disambiguationData":[OSD([subQ0,sQuery(id+"F15.wireOp",EDGE,"E20.15.0"),sQuery(id+"F15.wireOp",EDGE,"E20.15.1"),sQuery(id+"F15.wireOp",EDGE,"E20.15.2"),sQuery(id+"F15.wireOp",EDGE,"E20.15.3")])],"isStart":false}),makeQuery(id+"F16.opExtrude","CAP_FACE",FACE,{"disambiguationData":[OSD([subQ0,sQuery(id+"F15.wireOp",EDGE,"E20.16.0"),sQuery(id+"F15.wireOp",EDGE,"E20.16.1"),sQuery(id+"F15.wireOp",EDGE,"E20.16.2"),sQuery(id+"F15.wireOp",EDGE,"E20.16.3")])],"isStart":false}),makeQuery(id+"F16.opExtrude","CAP_FACE",FACE,{"disambiguationData":[OSD([subQ0,sQuery(id+"F15.wireOp",EDGE,"E20.17.0"),sQuery(id+"F15.wireOp",EDGE,"E20.17.1"),sQuery(id+"F15.wireOp",EDGE,"E20.17.2"),sQuery(id+"F15.wireOp",EDGE,"E20.17.3")])],"isStart":false}),makeQuery(id+"F16.opExtrude","CAP_FACE",FACE,{"disambiguationData":[OSD([subQ0,sQuery(id+"F15.wireOp",EDGE,"E20.18.0"),sQuery(id+"F15.wireOp",EDGE,"E20.18.1"),sQuery(id+"F15.wireOp",EDGE,"E20.18.2"),sQuery(id+"F15.wireOp",EDGE,"E20.18.3")])],"isStart":false}),makeQuery(id+"F16.opExtrude","CAP_FACE",FACE,{"disambiguationData":[OSD([subQ0,sQuery(id+"F15.wireOp",EDGE,"E20.19.0"),sQuery(id+"F15.wireOp",EDGE,"E20.19.1"),sQuery(id+"F15.wireOp",EDGE,"E20.19.2"),sQuery(id+"F15.wireOp",EDGE,"E20.19.3")])],"isStart":false}),makeQuery(id+"F16.opExtrude","CAP_FACE",FACE,{"disambiguationData":[OSD([subQ0,sQuery(id+"F15.wireOp",EDGE,"E20.20.0"),sQuery(id+"F15.wireOp",EDGE,"E20.20.1"),sQuery(id+"F15.wireOp",EDGE,"E20.20.2"),sQuery(id+"F15.wireOp",EDGE,"E20.20.3")])],"isStart":false}),makeQuery(id+"F16.opExtrude","CAP_FACE",FACE,{"disambiguationData":[OSD([subQ0,sQuery(id+"F15.wireOp",EDGE,"E20.21.0"),sQuery(id+"F15.wireOp",EDGE,"E20.21.1"),sQuery(id+"F15.wireOp",EDGE,"E20.21.2"),sQuery(id+"F15.wireOp",EDGE,"E20.21.3")])],"isStart":false}),makeQuery(id+"F16.opExtrude","CAP_FACE",FACE,{"disambiguationData":[OSD([subQ0,sQuery(id+"F15.wireOp",EDGE,"E20.22.0"),sQuery(id+"F15.wireOp",EDGE,"E20.22.1"),sQuery(id+"F15.wireOp",EDGE,"E20.22.2"),sQuery(id+"F15.wireOp",EDGE,"E20.22.3")])],"isStart":false}),makeQuery(id+"F16.opExtrude","CAP_FACE",FACE,{"disambiguationData":[OSD([subQ0,sQuery(id+"F15.wireOp",EDGE,"E20.23.0"),sQuery(id+"F15.wireOp",EDGE,"E20.23.1"),sQuery(id+"F15.wireOp",EDGE,"E20.23.2"),sQuery(id+"F15.wireOp",EDGE,"E20.23.3")])],"isStart":false})]});}
            var sketch = newSketch(context, id + "F20", { "sketchPlane" : qUnion([Q0])});
            skLineSegment(sketch, "E21", {"start": v(-25.4, 265.49) * mm, "end": v(-25.4, 292.1) * mm});
            skLineSegment(sketch, "E22", {"start": v(-25.4, 292.1) * mm, "end": v(25.4, 292.1) * mm});
            skLineSegment(sketch, "E23", {"start": v(25.4, 292.1) * mm, "end": v(25.4, 292.1) * mm});
            skLineSegment(sketch, "E24", {"start": v(25.4, 292.1) * mm, "end": v(25.4, 265.49) * mm});
            skArc(sketch, "E25", {"start": v(-25.4, 265.49) * mm, "mid": v(0, 266.7) * mm, "end": v(25.4, 265.49) * mm});
            skArc(sketch, "E26.1.0", {"start": v(-93.25, 249.87) * mm, "mid": v(-69.03, 257.61) * mm, "end": v(-44.18, 263.02) * mm});
            skLineSegment(sketch, "E26.1.1", {"start": v(-93.25, 249.87) * mm, "end": v(-100.14, 275.57) * mm});
            skLineSegment(sketch, "E26.1.2", {"start": v(-100.14, 275.57) * mm, "end": v(-51.07, 288.72) * mm});
            skLineSegment(sketch, "E26.1.3", {"start": v(-51.07, 288.72) * mm, "end": v(-44.18, 263.02) * mm});
            skArc(sketch, "E26.2.0", {"start": v(-154.74, 217.22) * mm, "mid": v(-133.35, 230.97) * mm, "end": v(-110.75, 242.62) * mm});
            skLineSegment(sketch, "E26.2.1", {"start": v(-154.74, 217.22) * mm, "end": v(-168.05, 240.27) * mm});
            skLineSegment(sketch, "E26.2.2", {"start": v(-168.05, 240.27) * mm, "end": v(-124.05, 265.67) * mm});
            skLineSegment(sketch, "E26.2.3", {"start": v(-124.05, 265.67) * mm, "end": v(-110.75, 242.62) * mm});
            skArc(sketch, "E26.3.0", {"start": v(-205.69, 169.77) * mm, "mid": v(-188.59, 188.59) * mm, "end": v(-169.77, 205.69) * mm});
            skLineSegment(sketch, "E26.3.1", {"start": v(-205.69, 169.77) * mm, "end": v(-224.5, 188.59) * mm});
            skLineSegment(sketch, "E26.3.2", {"start": v(-224.5, 188.59) * mm, "end": v(-188.59, 224.5) * mm});
            skLineSegment(sketch, "E26.3.3", {"start": v(-188.59, 224.5) * mm, "end": v(-169.77, 205.69) * mm});
            skArc(sketch, "E26.4.0", {"start": v(-242.62, 110.75) * mm, "mid": v(-230.97, 133.35) * mm, "end": v(-217.22, 154.74) * mm});
            skLineSegment(sketch, "E26.4.1", {"start": v(-242.62, 110.75) * mm, "end": v(-265.67, 124.05) * mm});
            skLineSegment(sketch, "E26.4.2", {"start": v(-265.67, 124.05) * mm, "end": v(-240.27, 168.05) * mm});
            skLineSegment(sketch, "E26.4.3", {"start": v(-240.27, 168.05) * mm, "end": v(-217.22, 154.74) * mm});
            skArc(sketch, "E26.5.0", {"start": v(-263.02, 44.18) * mm, "mid": v(-257.61, 69.03) * mm, "end": v(-249.87, 93.25) * mm});
            skLineSegment(sketch, "E26.5.1", {"start": v(-263.02, 44.18) * mm, "end": v(-288.72, 51.07) * mm});
            skLineSegment(sketch, "E26.5.2", {"start": v(-288.72, 51.07) * mm, "end": v(-275.57, 100.14) * mm});
            skLineSegment(sketch, "E26.5.3", {"start": v(-275.57, 100.14) * mm, "end": v(-249.87, 93.25) * mm});
            skArc(sketch, "E26.6.0", {"start": v(-265.49, -25.4) * mm, "mid": v(-266.7, 0) * mm, "end": v(-265.49, 25.4) * mm});
            skLineSegment(sketch, "E26.6.1", {"start": v(-265.49, -25.4) * mm, "end": v(-292.1, -25.4) * mm});
            skLineSegment(sketch, "E26.6.2", {"start": v(-292.1, -25.4) * mm, "end": v(-292.1, 25.4) * mm});
            skLineSegment(sketch, "E26.6.3", {"start": v(-292.1, 25.4) * mm, "end": v(-265.49, 25.4) * mm});
            skArc(sketch, "E26.7.0", {"start": v(-249.87, -93.25) * mm, "mid": v(-257.61, -69.03) * mm, "end": v(-263.02, -44.18) * mm});
            skLineSegment(sketch, "E26.7.1", {"start": v(-249.87, -93.25) * mm, "end": v(-275.57, -100.14) * mm});
            skLineSegment(sketch, "E26.7.2", {"start": v(-275.57, -100.14) * mm, "end": v(-288.72, -51.07) * mm});
            skLineSegment(sketch, "E26.7.3", {"start": v(-288.72, -51.07) * mm, "end": v(-263.02, -44.18) * mm});
            skArc(sketch, "E26.8.0", {"start": v(-217.22, -154.74) * mm, "mid": v(-230.97, -133.35) * mm, "end": v(-242.62, -110.75) * mm});
            skLineSegment(sketch, "E26.8.1", {"start": v(-217.22, -154.74) * mm, "end": v(-240.27, -168.05) * mm});
            skLineSegment(sketch, "E26.8.2", {"start": v(-240.27, -168.05) * mm, "end": v(-265.67, -124.05) * mm});
            skLineSegment(sketch, "E26.8.3", {"start": v(-265.67, -124.05) * mm, "end": v(-242.62, -110.75) * mm});
            skArc(sketch, "E26.9.0", {"start": v(-169.77, -205.69) * mm, "mid": v(-188.59, -188.59) * mm, "end": v(-205.69, -169.77) * mm});
            skLineSegment(sketch, "E26.9.1", {"start": v(-169.77, -205.69) * mm, "end": v(-188.59, -224.5) * mm});
            skLineSegment(sketch, "E26.9.2", {"start": v(-188.59, -224.5) * mm, "end": v(-224.5, -188.59) * mm});
            skLineSegment(sketch, "E26.9.3", {"start": v(-224.5, -188.59) * mm, "end": v(-205.69, -169.77) * mm});
            skArc(sketch, "E26.10.0", {"start": v(-110.75, -242.62) * mm, "mid": v(-133.35, -230.97) * mm, "end": v(-154.74, -217.22) * mm});
            skLineSegment(sketch, "E26.10.1", {"start": v(-110.75, -242.62) * mm, "end": v(-124.05, -265.67) * mm});
            skLineSegment(sketch, "E26.10.2", {"start": v(-124.05, -265.67) * mm, "end": v(-168.05, -240.27) * mm});
            skLineSegment(sketch, "E26.10.3", {"start": v(-168.05, -240.27) * mm, "end": v(-154.74, -217.22) * mm});
            skArc(sketch, "E26.11.0", {"start": v(-44.18, -263.02) * mm, "mid": v(-69.03, -257.61) * mm, "end": v(-93.25, -249.87) * mm});
            skLineSegment(sketch, "E26.11.1", {"start": v(-44.18, -263.02) * mm, "end": v(-51.07, -288.72) * mm});
            skLineSegment(sketch, "E26.11.2", {"start": v(-51.07, -288.72) * mm, "end": v(-100.14, -275.57) * mm});
            skLineSegment(sketch, "E26.11.3", {"start": v(-100.14, -275.57) * mm, "end": v(-93.25, -249.87) * mm});
            skArc(sketch, "E26.12.0", {"start": v(25.4, -265.49) * mm, "mid": v(0, -266.7) * mm, "end": v(-25.4, -265.49) * mm});
            skLineSegment(sketch, "E26.12.1", {"start": v(25.4, -265.49) * mm, "end": v(25.4, -292.1) * mm});
            skLineSegment(sketch, "E26.12.2", {"start": v(25.4, -292.1) * mm, "end": v(-25.4, -292.1) * mm});
            skLineSegment(sketch, "E26.12.3", {"start": v(-25.4, -292.1) * mm, "end": v(-25.4, -265.49) * mm});
            skArc(sketch, "E26.13.0", {"start": v(93.25, -249.87) * mm, "mid": v(69.03, -257.61) * mm, "end": v(44.18, -263.02) * mm});
            skLineSegment(sketch, "E26.13.1", {"start": v(93.25, -249.87) * mm, "end": v(100.14, -275.57) * mm});
            skLineSegment(sketch, "E26.13.2", {"start": v(100.14, -275.57) * mm, "end": v(51.07, -288.72) * mm});
            skLineSegment(sketch, "E26.13.3", {"start": v(51.07, -288.72) * mm, "end": v(44.18, -263.02) * mm});
            skArc(sketch, "E26.14.0", {"start": v(154.74, -217.22) * mm, "mid": v(133.35, -230.97) * mm, "end": v(110.75, -242.62) * mm});
            skLineSegment(sketch, "E26.14.1", {"start": v(154.74, -217.22) * mm, "end": v(168.05, -240.27) * mm});
            skLineSegment(sketch, "E26.14.2", {"start": v(168.05, -240.27) * mm, "end": v(124.05, -265.67) * mm});
            skLineSegment(sketch, "E26.14.3", {"start": v(124.05, -265.67) * mm, "end": v(110.75, -242.62) * mm});
            skArc(sketch, "E26.15.0", {"start": v(205.69, -169.77) * mm, "mid": v(188.59, -188.59) * mm, "end": v(169.77, -205.69) * mm});
            skLineSegment(sketch, "E26.15.1", {"start": v(205.69, -169.77) * mm, "end": v(224.5, -188.59) * mm});
            skLineSegment(sketch, "E26.15.2", {"start": v(224.5, -188.59) * mm, "end": v(188.59, -224.5) * mm});
            skLineSegment(sketch, "E26.15.3", {"start": v(188.59, -224.5) * mm, "end": v(169.77, -205.69) * mm});
            skArc(sketch, "E26.16.0", {"start": v(242.62, -110.75) * mm, "mid": v(230.97, -133.35) * mm, "end": v(217.22, -154.74) * mm});
            skLineSegment(sketch, "E26.16.1", {"start": v(242.62, -110.75) * mm, "end": v(265.67, -124.05) * mm});
            skLineSegment(sketch, "E26.16.2", {"start": v(265.67, -124.05) * mm, "end": v(240.27, -168.05) * mm});
            skLineSegment(sketch, "E26.16.3", {"start": v(240.27, -168.05) * mm, "end": v(217.22, -154.74) * mm});
            skArc(sketch, "E26.17.0", {"start": v(263.02, -44.18) * mm, "mid": v(257.61, -69.03) * mm, "end": v(249.87, -93.25) * mm});
            skLineSegment(sketch, "E26.17.1", {"start": v(263.02, -44.18) * mm, "end": v(288.72, -51.07) * mm});
            skLineSegment(sketch, "E26.17.2", {"start": v(288.72, -51.07) * mm, "end": v(275.57, -100.14) * mm});
            skLineSegment(sketch, "E26.17.3", {"start": v(275.57, -100.14) * mm, "end": v(249.87, -93.25) * mm});
            skArc(sketch, "E26.18.0", {"start": v(265.49, 25.4) * mm, "mid": v(266.7, 0) * mm, "end": v(265.49, -25.4) * mm});
            skLineSegment(sketch, "E26.18.1", {"start": v(265.49, 25.4) * mm, "end": v(292.1, 25.4) * mm});
            skLineSegment(sketch, "E26.18.2", {"start": v(292.1, 25.4) * mm, "end": v(292.1, -25.4) * mm});
            skLineSegment(sketch, "E26.18.3", {"start": v(292.1, -25.4) * mm, "end": v(265.49, -25.4) * mm});
            skArc(sketch, "E26.19.0", {"start": v(249.87, 93.25) * mm, "mid": v(257.61, 69.03) * mm, "end": v(263.02, 44.18) * mm});
            skLineSegment(sketch, "E26.19.1", {"start": v(249.87, 93.25) * mm, "end": v(275.57, 100.14) * mm});
            skLineSegment(sketch, "E26.19.2", {"start": v(275.57, 100.14) * mm, "end": v(288.72, 51.07) * mm});
            skLineSegment(sketch, "E26.19.3", {"start": v(288.72, 51.07) * mm, "end": v(263.02, 44.18) * mm});
            skArc(sketch, "E26.20.0", {"start": v(217.22, 154.74) * mm, "mid": v(230.97, 133.35) * mm, "end": v(242.62, 110.75) * mm});
            skLineSegment(sketch, "E26.20.1", {"start": v(217.22, 154.74) * mm, "end": v(240.27, 168.05) * mm});
            skLineSegment(sketch, "E26.20.2", {"start": v(240.27, 168.05) * mm, "end": v(265.67, 124.05) * mm});
            skLineSegment(sketch, "E26.20.3", {"start": v(265.67, 124.05) * mm, "end": v(242.62, 110.75) * mm});
            skArc(sketch, "E26.21.0", {"start": v(169.77, 205.69) * mm, "mid": v(188.59, 188.59) * mm, "end": v(205.69, 169.77) * mm});
            skLineSegment(sketch, "E26.21.1", {"start": v(169.77, 205.69) * mm, "end": v(188.59, 224.5) * mm});
            skLineSegment(sketch, "E26.21.2", {"start": v(188.59, 224.5) * mm, "end": v(224.5, 188.59) * mm});
            skLineSegment(sketch, "E26.21.3", {"start": v(224.5, 188.59) * mm, "end": v(205.69, 169.77) * mm});
            skArc(sketch, "E26.22.0", {"start": v(110.75, 242.62) * mm, "mid": v(133.35, 230.97) * mm, "end": v(154.74, 217.22) * mm});
            skLineSegment(sketch, "E26.22.1", {"start": v(110.75, 242.62) * mm, "end": v(124.05, 265.67) * mm});
            skLineSegment(sketch, "E26.22.2", {"start": v(124.05, 265.67) * mm, "end": v(168.05, 240.27) * mm});
            skLineSegment(sketch, "E26.22.3", {"start": v(168.05, 240.27) * mm, "end": v(154.74, 217.22) * mm});
            skArc(sketch, "E26.23.0", {"start": v(44.18, 263.02) * mm, "mid": v(69.03, 257.61) * mm, "end": v(93.25, 249.87) * mm});
            skLineSegment(sketch, "E26.23.1", {"start": v(44.18, 263.02) * mm, "end": v(51.07, 288.72) * mm});
            skLineSegment(sketch, "E26.23.2", {"start": v(51.07, 288.72) * mm, "end": v(100.14, 275.57) * mm});
            skLineSegment(sketch, "E26.23.3", {"start": v(100.14, 275.57) * mm, "end": v(93.25, 249.87) * mm});
            skSolve(sketch);
        }
        {
            var Q0;
            {var subQ1=sQuery(id+"F20.wireOp",EDGE,"E21");Q0=makeQuery(id+"F20.imprint","IMPRINT",FACE,{"disambiguationData":[TD([[makeQuery(id+"F20.imprint","IMPRINT",EDGE,{"derivedFrom":subQ1}),1.0]])]});}
            var Q1;
            Q1=makeQuery(id+"F20.imprint","IMPRINT",FACE,{"disambiguationData":[TD([[makeQuery(id+"F20.imprint","IMPRINT",EDGE,{"derivedFrom":sQuery(id+"F20.wireOp",EDGE,"E26.23.0")}),1.0]])]});
            var Q2;
            Q2=makeQuery(id+"F20.imprint","IMPRINT",FACE,{"disambiguationData":[TD([[makeQuery(id+"F20.imprint","IMPRINT",EDGE,{"derivedFrom":sQuery(id+"F20.wireOp",EDGE,"E26.22.0")}),1.0]])]});
            var Q3;
            Q3=makeQuery(id+"F20.imprint","IMPRINT",FACE,{"disambiguationData":[TD([[makeQuery(id+"F20.imprint","IMPRINT",EDGE,{"derivedFrom":sQuery(id+"F20.wireOp",EDGE,"E26.21.0")}),1.0]])]});
            var Q4;
            {var subQ0=sQuery(id+"F20.wireOp",EDGE,"E26.20.1");Q4=makeQuery(id+"F20.imprint","IMPRINT",FACE,{"disambiguationData":[TD([[makeQuery(id+"F20.imprint","IMPRINT",EDGE,{"derivedFrom":subQ0}),1.0]])]});}
            var Q5;
            Q5=makeQuery(id+"F20.imprint","IMPRINT",FACE,{"disambiguationData":[TD([[makeQuery(id+"F20.imprint","IMPRINT",EDGE,{"derivedFrom":sQuery(id+"F20.wireOp",EDGE,"E26.19.0")}),1.0]])]});
            var Q6;
            Q6=makeQuery(id+"F20.imprint","IMPRINT",FACE,{"disambiguationData":[TD([[makeQuery(id+"F20.imprint","IMPRINT",EDGE,{"derivedFrom":sQuery(id+"F20.wireOp",EDGE,"E26.17.0")}),1.0]])]});
            var Q7;
            {var subQ0=sQuery(id+"F20.wireOp",EDGE,"E26.16.1");Q7=makeQuery(id+"F20.imprint","IMPRINT",FACE,{"disambiguationData":[TD([[makeQuery(id+"F20.imprint","IMPRINT",EDGE,{"derivedFrom":subQ0}),1.0]])]});}
            var Q8;
            Q8=makeQuery(id+"F20.imprint","IMPRINT",FACE,{"disambiguationData":[TD([[makeQuery(id+"F20.imprint","IMPRINT",EDGE,{"derivedFrom":sQuery(id+"F20.wireOp",EDGE,"E26.15.0")}),1.0]])]});
            var Q9;
            Q9=makeQuery(id+"F20.imprint","IMPRINT",FACE,{"disambiguationData":[TD([[makeQuery(id+"F20.imprint","IMPRINT",EDGE,{"derivedFrom":sQuery(id+"F20.wireOp",EDGE,"E26.18.0")}),1.0]])]});
            var Q10;
            Q10=makeQuery(id+"F20.imprint","IMPRINT",FACE,{"disambiguationData":[TD([[makeQuery(id+"F20.imprint","IMPRINT",EDGE,{"derivedFrom":sQuery(id+"F20.wireOp",EDGE,"E26.14.0")}),1.0]])]});
            var Q11;
            Q11=makeQuery(id+"F20.imprint","IMPRINT",FACE,{"disambiguationData":[TD([[makeQuery(id+"F20.imprint","IMPRINT",EDGE,{"derivedFrom":sQuery(id+"F20.wireOp",EDGE,"E26.13.0")}),1.0]])]});
            var Q12;
            {var subQ0=sQuery(id+"F20.wireOp",EDGE,"E26.12.1");Q12=makeQuery(id+"F20.imprint","IMPRINT",FACE,{"disambiguationData":[TD([[makeQuery(id+"F20.imprint","IMPRINT",EDGE,{"derivedFrom":subQ0}),1.0]])]});}
            var Q13;
            Q13=makeQuery(id+"F20.imprint","IMPRINT",FACE,{"disambiguationData":[TD([[makeQuery(id+"F20.imprint","IMPRINT",EDGE,{"derivedFrom":sQuery(id+"F20.wireOp",EDGE,"E26.10.0")}),1.0]])]});
            var Q14;
            Q14=makeQuery(id+"F20.imprint","IMPRINT",FACE,{"disambiguationData":[TD([[makeQuery(id+"F20.imprint","IMPRINT",EDGE,{"derivedFrom":sQuery(id+"F20.wireOp",EDGE,"E26.9.0")}),1.0]])]});
            var Q15;
            Q15=makeQuery(id+"F20.imprint","IMPRINT",FACE,{"disambiguationData":[TD([[makeQuery(id+"F20.imprint","IMPRINT",EDGE,{"derivedFrom":sQuery(id+"F20.wireOp",EDGE,"E26.11.0")}),1.0]])]});
            var Q16;
            {var subQ0=sQuery(id+"F20.wireOp",EDGE,"E26.8.1");Q16=makeQuery(id+"F20.imprint","IMPRINT",FACE,{"disambiguationData":[TD([[makeQuery(id+"F20.imprint","IMPRINT",EDGE,{"derivedFrom":subQ0}),1.0]])]});}
            var Q17;
            Q17=makeQuery(id+"F20.imprint","IMPRINT",FACE,{"disambiguationData":[TD([[makeQuery(id+"F20.imprint","IMPRINT",EDGE,{"derivedFrom":sQuery(id+"F20.wireOp",EDGE,"E26.6.0")}),1.0]])]});
            var Q18;
            Q18=makeQuery(id+"F20.imprint","IMPRINT",FACE,{"disambiguationData":[TD([[makeQuery(id+"F20.imprint","IMPRINT",EDGE,{"derivedFrom":sQuery(id+"F20.wireOp",EDGE,"E26.7.0")}),1.0]])]});
            var Q19;
            Q19=makeQuery(id+"F20.imprint","IMPRINT",FACE,{"disambiguationData":[TD([[makeQuery(id+"F20.imprint","IMPRINT",EDGE,{"derivedFrom":sQuery(id+"F20.wireOp",EDGE,"E26.5.0")}),1.0]])]});
            var Q20;
            Q20=makeQuery(id+"F20.imprint","IMPRINT",FACE,{"disambiguationData":[TD([[makeQuery(id+"F20.imprint","IMPRINT",EDGE,{"derivedFrom":sQuery(id+"F20.wireOp",EDGE,"E26.3.0")}),1.0]])]});
            var Q21;
            Q21=makeQuery(id+"F20.imprint","IMPRINT",FACE,{"disambiguationData":[TD([[makeQuery(id+"F20.imprint","IMPRINT",EDGE,{"derivedFrom":sQuery(id+"F20.wireOp",EDGE,"E26.2.0")}),1.0]])]});
            var Q22;
            {var subQ0=sQuery(id+"F20.wireOp",EDGE,"E26.4.1");Q22=makeQuery(id+"F20.imprint","IMPRINT",FACE,{"disambiguationData":[TD([[makeQuery(id+"F20.imprint","IMPRINT",EDGE,{"derivedFrom":subQ0}),1.0]])]});}
            var Q23;
            Q23=makeQuery(id+"F20.imprint","IMPRINT",FACE,{"disambiguationData":[TD([[makeQuery(id+"F20.imprint","IMPRINT",EDGE,{"derivedFrom":sQuery(id+"F20.wireOp",EDGE,"E26.1.0")}),1.0]])]});
            extrude(context, id + "F21", {"entities" : qUnion([Q0, Q1, Q2, Q3, Q4, Q5, Q6, Q7, Q8, Q9, Q10, Q11, Q12, Q13, Q14, Q15, Q16, Q17, Q18, Q19, Q20, Q21, Q22, Q23]), "operationType" : NewBodyOperationType.ADD, "depth" : 12.7 * mm, "offsetDistance" : 25.4 * mm});
        }
        {
            var Q0;
            Q0=makeQuery(id+"F1.opRevolve","SWEPT_FACE",FACE,{"disambiguationData":[OSD([sQuery(id+"F0.wireOp",EDGE,"E0")])]});
            var sketch = newSketch(context, id + "F22", { "sketchPlane" : qUnion([Q0])});
            skLineSegment(sketch, "E27", {"start": v(-25.4, 265.49) * mm, "end": v(-25.4, 292.1) * mm});
            skLineSegment(sketch, "E28", {"start": v(-25.4, 292.1) * mm, "end": v(25.4, 292.1) * mm});
            skLineSegment(sketch, "E29", {"start": v(25.4, 292.1) * mm, "end": v(25.4, 265.49) * mm});
            skArc(sketch, "E30", {"start": v(-25.4, 265.49) * mm, "mid": v(0, 266.7) * mm, "end": v(25.4, 265.49) * mm});
            skArc(sketch, "E31.1.0", {"start": v(-93.25, 249.87) * mm, "mid": v(-69.03, 257.61) * mm, "end": v(-44.18, 263.02) * mm});
            skLineSegment(sketch, "E31.1.1", {"start": v(-100.14, 275.57) * mm, "end": v(-51.07, 288.72) * mm});
            skLineSegment(sketch, "E31.1.2", {"start": v(-51.07, 288.72) * mm, "end": v(-44.18, 263.02) * mm});
            skLineSegment(sketch, "E31.1.3", {"start": v(-93.25, 249.87) * mm, "end": v(-100.14, 275.57) * mm});
            skArc(sketch, "E31.2.0", {"start": v(-154.74, 217.22) * mm, "mid": v(-133.35, 230.97) * mm, "end": v(-110.75, 242.62) * mm});
            skLineSegment(sketch, "E31.2.1", {"start": v(-168.05, 240.27) * mm, "end": v(-124.05, 265.67) * mm});
            skLineSegment(sketch, "E31.2.2", {"start": v(-124.05, 265.67) * mm, "end": v(-110.75, 242.62) * mm});
            skLineSegment(sketch, "E31.2.3", {"start": v(-154.74, 217.22) * mm, "end": v(-168.05, 240.27) * mm});
            skArc(sketch, "E31.3.0", {"start": v(-205.69, 169.77) * mm, "mid": v(-188.59, 188.59) * mm, "end": v(-169.77, 205.69) * mm});
            skLineSegment(sketch, "E31.3.1", {"start": v(-224.5, 188.59) * mm, "end": v(-188.59, 224.5) * mm});
            skLineSegment(sketch, "E31.3.2", {"start": v(-188.59, 224.5) * mm, "end": v(-169.77, 205.69) * mm});
            skLineSegment(sketch, "E31.3.3", {"start": v(-205.69, 169.77) * mm, "end": v(-224.5, 188.59) * mm});
            skArc(sketch, "E31.4.0", {"start": v(-242.62, 110.75) * mm, "mid": v(-230.97, 133.35) * mm, "end": v(-217.22, 154.74) * mm});
            skLineSegment(sketch, "E31.4.1", {"start": v(-265.67, 124.05) * mm, "end": v(-240.27, 168.05) * mm});
            skLineSegment(sketch, "E31.4.2", {"start": v(-240.27, 168.05) * mm, "end": v(-217.22, 154.74) * mm});
            skLineSegment(sketch, "E31.4.3", {"start": v(-242.62, 110.75) * mm, "end": v(-265.67, 124.05) * mm});
            skArc(sketch, "E31.5.0", {"start": v(-263.02, 44.18) * mm, "mid": v(-257.61, 69.03) * mm, "end": v(-249.87, 93.25) * mm});
            skLineSegment(sketch, "E31.5.1", {"start": v(-288.72, 51.07) * mm, "end": v(-275.57, 100.14) * mm});
            skLineSegment(sketch, "E31.5.2", {"start": v(-275.57, 100.14) * mm, "end": v(-249.87, 93.25) * mm});
            skLineSegment(sketch, "E31.5.3", {"start": v(-263.02, 44.18) * mm, "end": v(-288.72, 51.07) * mm});
            skArc(sketch, "E31.6.0", {"start": v(-265.49, -25.4) * mm, "mid": v(-266.7, 0) * mm, "end": v(-265.49, 25.4) * mm});
            skLineSegment(sketch, "E31.6.1", {"start": v(-292.1, -25.4) * mm, "end": v(-292.1, 25.4) * mm});
            skLineSegment(sketch, "E31.6.2", {"start": v(-292.1, 25.4) * mm, "end": v(-265.49, 25.4) * mm});
            skLineSegment(sketch, "E31.6.3", {"start": v(-265.49, -25.4) * mm, "end": v(-292.1, -25.4) * mm});
            skArc(sketch, "E31.7.0", {"start": v(-249.87, -93.25) * mm, "mid": v(-257.61, -69.03) * mm, "end": v(-263.02, -44.18) * mm});
            skLineSegment(sketch, "E31.7.1", {"start": v(-275.57, -100.14) * mm, "end": v(-288.72, -51.07) * mm});
            skLineSegment(sketch, "E31.7.2", {"start": v(-288.72, -51.07) * mm, "end": v(-263.02, -44.18) * mm});
            skLineSegment(sketch, "E31.7.3", {"start": v(-249.87, -93.25) * mm, "end": v(-275.57, -100.14) * mm});
            skArc(sketch, "E31.8.0", {"start": v(-217.22, -154.74) * mm, "mid": v(-230.97, -133.35) * mm, "end": v(-242.62, -110.75) * mm});
            skLineSegment(sketch, "E31.8.1", {"start": v(-240.27, -168.05) * mm, "end": v(-265.67, -124.05) * mm});
            skLineSegment(sketch, "E31.8.2", {"start": v(-265.67, -124.05) * mm, "end": v(-242.62, -110.75) * mm});
            skLineSegment(sketch, "E31.8.3", {"start": v(-217.22, -154.74) * mm, "end": v(-240.27, -168.05) * mm});
            skArc(sketch, "E31.9.0", {"start": v(-169.77, -205.69) * mm, "mid": v(-188.59, -188.59) * mm, "end": v(-205.69, -169.77) * mm});
            skLineSegment(sketch, "E31.9.1", {"start": v(-188.59, -224.5) * mm, "end": v(-224.5, -188.59) * mm});
            skLineSegment(sketch, "E31.9.2", {"start": v(-224.5, -188.59) * mm, "end": v(-205.69, -169.77) * mm});
            skLineSegment(sketch, "E31.9.3", {"start": v(-169.77, -205.69) * mm, "end": v(-188.59, -224.5) * mm});
            skArc(sketch, "E31.10.0", {"start": v(-110.75, -242.62) * mm, "mid": v(-133.35, -230.97) * mm, "end": v(-154.74, -217.22) * mm});
            skLineSegment(sketch, "E31.10.1", {"start": v(-124.05, -265.67) * mm, "end": v(-168.05, -240.27) * mm});
            skLineSegment(sketch, "E31.10.2", {"start": v(-168.05, -240.27) * mm, "end": v(-154.74, -217.22) * mm});
            skLineSegment(sketch, "E31.10.3", {"start": v(-110.75, -242.62) * mm, "end": v(-124.05, -265.67) * mm});
            skArc(sketch, "E31.11.0", {"start": v(-44.18, -263.02) * mm, "mid": v(-69.03, -257.61) * mm, "end": v(-93.25, -249.87) * mm});
            skLineSegment(sketch, "E31.11.1", {"start": v(-51.07, -288.72) * mm, "end": v(-100.14, -275.57) * mm});
            skLineSegment(sketch, "E31.11.2", {"start": v(-100.14, -275.57) * mm, "end": v(-93.25, -249.87) * mm});
            skLineSegment(sketch, "E31.11.3", {"start": v(-44.18, -263.02) * mm, "end": v(-51.07, -288.72) * mm});
            skArc(sketch, "E31.12.0", {"start": v(25.4, -265.49) * mm, "mid": v(0, -266.7) * mm, "end": v(-25.4, -265.49) * mm});
            skLineSegment(sketch, "E31.12.1", {"start": v(25.4, -292.1) * mm, "end": v(-25.4, -292.1) * mm});
            skLineSegment(sketch, "E31.12.2", {"start": v(-25.4, -292.1) * mm, "end": v(-25.4, -265.49) * mm});
            skLineSegment(sketch, "E31.12.3", {"start": v(25.4, -265.49) * mm, "end": v(25.4, -292.1) * mm});
            skArc(sketch, "E31.13.0", {"start": v(93.25, -249.87) * mm, "mid": v(69.03, -257.61) * mm, "end": v(44.18, -263.02) * mm});
            skLineSegment(sketch, "E31.13.1", {"start": v(100.14, -275.57) * mm, "end": v(51.07, -288.72) * mm});
            skLineSegment(sketch, "E31.13.2", {"start": v(51.07, -288.72) * mm, "end": v(44.18, -263.02) * mm});
            skLineSegment(sketch, "E31.13.3", {"start": v(93.25, -249.87) * mm, "end": v(100.14, -275.57) * mm});
            skArc(sketch, "E31.14.0", {"start": v(154.74, -217.22) * mm, "mid": v(133.35, -230.97) * mm, "end": v(110.75, -242.62) * mm});
            skLineSegment(sketch, "E31.14.1", {"start": v(168.05, -240.27) * mm, "end": v(124.05, -265.67) * mm});
            skLineSegment(sketch, "E31.14.2", {"start": v(124.05, -265.67) * mm, "end": v(110.75, -242.62) * mm});
            skLineSegment(sketch, "E31.14.3", {"start": v(154.74, -217.22) * mm, "end": v(168.05, -240.27) * mm});
            skArc(sketch, "E31.15.0", {"start": v(205.69, -169.77) * mm, "mid": v(188.59, -188.59) * mm, "end": v(169.77, -205.69) * mm});
            skLineSegment(sketch, "E31.15.1", {"start": v(224.5, -188.59) * mm, "end": v(188.59, -224.5) * mm});
            skLineSegment(sketch, "E31.15.2", {"start": v(188.59, -224.5) * mm, "end": v(169.77, -205.69) * mm});
            skLineSegment(sketch, "E31.15.3", {"start": v(205.69, -169.77) * mm, "end": v(224.5, -188.59) * mm});
            skArc(sketch, "E31.16.0", {"start": v(242.62, -110.75) * mm, "mid": v(230.97, -133.35) * mm, "end": v(217.22, -154.74) * mm});
            skLineSegment(sketch, "E31.16.1", {"start": v(265.67, -124.05) * mm, "end": v(240.27, -168.05) * mm});
            skLineSegment(sketch, "E31.16.2", {"start": v(240.27, -168.05) * mm, "end": v(217.22, -154.74) * mm});
            skLineSegment(sketch, "E31.16.3", {"start": v(242.62, -110.75) * mm, "end": v(265.67, -124.05) * mm});
            skArc(sketch, "E31.17.0", {"start": v(263.02, -44.18) * mm, "mid": v(257.61, -69.03) * mm, "end": v(249.87, -93.25) * mm});
            skLineSegment(sketch, "E31.17.1", {"start": v(288.72, -51.07) * mm, "end": v(275.57, -100.14) * mm});
            skLineSegment(sketch, "E31.17.2", {"start": v(275.57, -100.14) * mm, "end": v(249.87, -93.25) * mm});
            skLineSegment(sketch, "E31.17.3", {"start": v(263.02, -44.18) * mm, "end": v(288.72, -51.07) * mm});
            skArc(sketch, "E31.18.0", {"start": v(265.49, 25.4) * mm, "mid": v(266.7, 0) * mm, "end": v(265.49, -25.4) * mm});
            skLineSegment(sketch, "E31.18.1", {"start": v(292.1, 25.4) * mm, "end": v(292.1, -25.4) * mm});
            skLineSegment(sketch, "E31.18.2", {"start": v(292.1, -25.4) * mm, "end": v(265.49, -25.4) * mm});
            skLineSegment(sketch, "E31.18.3", {"start": v(265.49, 25.4) * mm, "end": v(292.1, 25.4) * mm});
            skArc(sketch, "E31.19.0", {"start": v(249.87, 93.25) * mm, "mid": v(257.61, 69.03) * mm, "end": v(263.02, 44.18) * mm});
            skLineSegment(sketch, "E31.19.1", {"start": v(275.57, 100.14) * mm, "end": v(288.72, 51.07) * mm});
            skLineSegment(sketch, "E31.19.2", {"start": v(288.72, 51.07) * mm, "end": v(263.02, 44.18) * mm});
            skLineSegment(sketch, "E31.19.3", {"start": v(249.87, 93.25) * mm, "end": v(275.57, 100.14) * mm});
            skArc(sketch, "E31.20.0", {"start": v(217.22, 154.74) * mm, "mid": v(230.97, 133.35) * mm, "end": v(242.62, 110.75) * mm});
            skLineSegment(sketch, "E31.20.1", {"start": v(240.27, 168.05) * mm, "end": v(265.67, 124.05) * mm});
            skLineSegment(sketch, "E31.20.2", {"start": v(265.67, 124.05) * mm, "end": v(242.62, 110.75) * mm});
            skLineSegment(sketch, "E31.20.3", {"start": v(217.22, 154.74) * mm, "end": v(240.27, 168.05) * mm});
            skArc(sketch, "E31.21.0", {"start": v(169.77, 205.69) * mm, "mid": v(188.59, 188.59) * mm, "end": v(205.69, 169.77) * mm});
            skLineSegment(sketch, "E31.21.1", {"start": v(188.59, 224.5) * mm, "end": v(224.5, 188.59) * mm});
            skLineSegment(sketch, "E31.21.2", {"start": v(224.5, 188.59) * mm, "end": v(205.69, 169.77) * mm});
            skLineSegment(sketch, "E31.21.3", {"start": v(169.77, 205.69) * mm, "end": v(188.59, 224.5) * mm});
            skArc(sketch, "E31.22.0", {"start": v(110.75, 242.62) * mm, "mid": v(133.35, 230.97) * mm, "end": v(154.74, 217.22) * mm});
            skLineSegment(sketch, "E31.22.1", {"start": v(124.05, 265.67) * mm, "end": v(168.05, 240.27) * mm});
            skLineSegment(sketch, "E31.22.2", {"start": v(168.05, 240.27) * mm, "end": v(154.74, 217.22) * mm});
            skLineSegment(sketch, "E31.22.3", {"start": v(110.75, 242.62) * mm, "end": v(124.05, 265.67) * mm});
            skArc(sketch, "E31.23.0", {"start": v(44.18, 263.02) * mm, "mid": v(69.03, 257.61) * mm, "end": v(93.25, 249.87) * mm});
            skLineSegment(sketch, "E31.23.1", {"start": v(51.07, 288.72) * mm, "end": v(100.14, 275.57) * mm});
            skLineSegment(sketch, "E31.23.2", {"start": v(100.14, 275.57) * mm, "end": v(93.25, 249.87) * mm});
            skLineSegment(sketch, "E31.23.3", {"start": v(44.18, 263.02) * mm, "end": v(51.07, 288.72) * mm});
            skSolve(sketch);
        }
        {
            var Q0;
            Q0=makeQuery(id+"F22.imprint","IMPRINT",FACE,{"disambiguationData":[TD([[makeQuery(id+"F22.imprint","IMPRINT",EDGE,{"derivedFrom":sQuery(id+"F22.wireOp",EDGE,"E27")}),1.0]])]});
            var Q1;
            Q1=makeQuery(id+"F22.imprint","IMPRINT",FACE,{"disambiguationData":[TD([[makeQuery(id+"F22.imprint","IMPRINT",EDGE,{"derivedFrom":sQuery(id+"F22.wireOp",EDGE,"E31.1.0")}),1.0]])]});
            var Q2;
            Q2=makeQuery(id+"F22.imprint","IMPRINT",FACE,{"disambiguationData":[TD([[makeQuery(id+"F22.imprint","IMPRINT",EDGE,{"derivedFrom":sQuery(id+"F22.wireOp",EDGE,"E31.3.0")}),1.0]])]});
            var Q3;
            Q3=makeQuery(id+"F22.imprint","IMPRINT",FACE,{"disambiguationData":[TD([[makeQuery(id+"F22.imprint","IMPRINT",EDGE,{"derivedFrom":sQuery(id+"F22.wireOp",EDGE,"E31.2.0")}),1.0]])]});
            var Q4;
            Q4=makeQuery(id+"F22.imprint","IMPRINT",FACE,{"disambiguationData":[TD([[makeQuery(id+"F22.imprint","IMPRINT",EDGE,{"derivedFrom":sQuery(id+"F22.wireOp",EDGE,"E31.4.0")}),1.0]])]});
            var Q5;
            Q5=makeQuery(id+"F22.imprint","IMPRINT",FACE,{"disambiguationData":[TD([[makeQuery(id+"F22.imprint","IMPRINT",EDGE,{"derivedFrom":sQuery(id+"F22.wireOp",EDGE,"E31.6.0")}),1.0]])]});
            var Q6;
            Q6=makeQuery(id+"F22.imprint","IMPRINT",FACE,{"disambiguationData":[TD([[makeQuery(id+"F22.imprint","IMPRINT",EDGE,{"derivedFrom":sQuery(id+"F22.wireOp",EDGE,"E31.7.0")}),1.0]])]});
            var Q7;
            Q7=makeQuery(id+"F22.imprint","IMPRINT",FACE,{"disambiguationData":[TD([[makeQuery(id+"F22.imprint","IMPRINT",EDGE,{"derivedFrom":sQuery(id+"F22.wireOp",EDGE,"E31.5.0")}),1.0]])]});
            var Q8;
            Q8=makeQuery(id+"F22.imprint","IMPRINT",FACE,{"disambiguationData":[TD([[makeQuery(id+"F22.imprint","IMPRINT",EDGE,{"derivedFrom":sQuery(id+"F22.wireOp",EDGE,"E31.8.0")}),1.0]])]});
            var Q9;
            Q9=makeQuery(id+"F22.imprint","IMPRINT",FACE,{"disambiguationData":[TD([[makeQuery(id+"F22.imprint","IMPRINT",EDGE,{"derivedFrom":sQuery(id+"F22.wireOp",EDGE,"E31.9.0")}),1.0]])]});
            var Q10;
            Q10=makeQuery(id+"F22.imprint","IMPRINT",FACE,{"disambiguationData":[TD([[makeQuery(id+"F22.imprint","IMPRINT",EDGE,{"derivedFrom":sQuery(id+"F22.wireOp",EDGE,"E31.11.0")}),1.0]])]});
            var Q11;
            Q11=makeQuery(id+"F22.imprint","IMPRINT",FACE,{"disambiguationData":[TD([[makeQuery(id+"F22.imprint","IMPRINT",EDGE,{"derivedFrom":sQuery(id+"F22.wireOp",EDGE,"E31.12.0")}),1.0]])]});
            var Q12;
            Q12=makeQuery(id+"F22.imprint","IMPRINT",FACE,{"disambiguationData":[TD([[makeQuery(id+"F22.imprint","IMPRINT",EDGE,{"derivedFrom":sQuery(id+"F22.wireOp",EDGE,"E31.10.0")}),1.0]])]});
            var Q13;
            Q13=makeQuery(id+"F22.imprint","IMPRINT",FACE,{"disambiguationData":[TD([[makeQuery(id+"F22.imprint","IMPRINT",EDGE,{"derivedFrom":sQuery(id+"F22.wireOp",EDGE,"E31.14.0")}),1.0]])]});
            var Q14;
            Q14=makeQuery(id+"F22.imprint","IMPRINT",FACE,{"disambiguationData":[TD([[makeQuery(id+"F22.imprint","IMPRINT",EDGE,{"derivedFrom":sQuery(id+"F22.wireOp",EDGE,"E31.13.0")}),1.0]])]});
            var Q15;
            Q15=makeQuery(id+"F22.imprint","IMPRINT",FACE,{"disambiguationData":[TD([[makeQuery(id+"F22.imprint","IMPRINT",EDGE,{"derivedFrom":sQuery(id+"F22.wireOp",EDGE,"E31.15.0")}),1.0]])]});
            var Q16;
            Q16=makeQuery(id+"F22.imprint","IMPRINT",FACE,{"disambiguationData":[TD([[makeQuery(id+"F22.imprint","IMPRINT",EDGE,{"derivedFrom":sQuery(id+"F22.wireOp",EDGE,"E31.17.0")}),1.0]])]});
            var Q17;
            Q17=makeQuery(id+"F22.imprint","IMPRINT",FACE,{"disambiguationData":[TD([[makeQuery(id+"F22.imprint","IMPRINT",EDGE,{"derivedFrom":sQuery(id+"F22.wireOp",EDGE,"E31.16.0")}),1.0]])]});
            var Q18;
            Q18=makeQuery(id+"F22.imprint","IMPRINT",FACE,{"disambiguationData":[TD([[makeQuery(id+"F22.imprint","IMPRINT",EDGE,{"derivedFrom":sQuery(id+"F22.wireOp",EDGE,"E31.18.0")}),1.0]])]});
            var Q19;
            Q19=makeQuery(id+"F22.imprint","IMPRINT",FACE,{"disambiguationData":[TD([[makeQuery(id+"F22.imprint","IMPRINT",EDGE,{"derivedFrom":sQuery(id+"F22.wireOp",EDGE,"E31.20.0")}),1.0]])]});
            var Q20;
            Q20=makeQuery(id+"F22.imprint","IMPRINT",FACE,{"disambiguationData":[TD([[makeQuery(id+"F22.imprint","IMPRINT",EDGE,{"derivedFrom":sQuery(id+"F22.wireOp",EDGE,"E31.22.0")}),1.0]])]});
            var Q21;
            Q21=makeQuery(id+"F22.imprint","IMPRINT",FACE,{"disambiguationData":[TD([[makeQuery(id+"F22.imprint","IMPRINT",EDGE,{"derivedFrom":sQuery(id+"F22.wireOp",EDGE,"E31.23.0")}),1.0]])]});
            var Q22;
            Q22=makeQuery(id+"F22.imprint","IMPRINT",FACE,{"disambiguationData":[TD([[makeQuery(id+"F22.imprint","IMPRINT",EDGE,{"derivedFrom":sQuery(id+"F22.wireOp",EDGE,"E31.19.0")}),1.0]])]});
            var Q23;
            Q23=makeQuery(id+"F22.imprint","IMPRINT",FACE,{"disambiguationData":[TD([[makeQuery(id+"F22.imprint","IMPRINT",EDGE,{"derivedFrom":sQuery(id+"F22.wireOp",EDGE,"E31.21.0")}),1.0]])]});
            extrude(context, id + "F23", {"entities" : qUnion([Q0, Q1, Q2, Q3, Q4, Q5, Q6, Q7, Q8, Q9, Q10, Q11, Q12, Q13, Q14, Q15, Q16, Q17, Q18, Q19, Q20, Q21, Q22, Q23]), "operationType" : NewBodyOperationType.ADD, "oppositeDirection" : true, "depth" : 12.7 * mm, "offsetDistance" : 25.4 * mm});
        }
        {
            var Q0;
            {var subQ0=sQuery(id+"F2.wireOp",EDGE,"E6");var subQ10=sQuery(id+"F15.wireOp",EDGE,"E20.7.3");var subQ16=makeQuery(id+"F3.boolean.opBoolean","COPY",FACE,{"derivedFrom":makeQuery(id+"F3.opExtrude","CAP_FACE",FACE,{"disambiguationData":[OSD([subQ0])],"isStart":false})});var subQ17=sQuery(id+"F15.wireOp",EDGE,"E20.4.3");var subQ19=makeQuery(id+"F3.boolean.opBoolean","COPY",FACE,{"derivedFrom":makeQuery(id+"F3.opExtrude","SWEPT_FACE",FACE,{"disambiguationData":[OSD([subQ0])]})});var subQ20=sQuery(id+"F15.wireOp",EDGE,"E20.6.3");var subQ24=sQuery(id+"F15.wireOp",EDGE,"E20.5.3");var subQ35=sQuery(id+"F8.wireOp",EDGE,"E12.4.0");var subQ36=makeQuery(id+"F10.boolean.opBoolean","SPLIT",EDGE,{"disambiguationData":[TD([subQ19,subQ16,makeQuery(id+"F10.opExtrude","SWEPT_FACE",FACE,{"disambiguationData":[OSD([subQ35]),TDD([makeQuery(id+"F8.imprint","IMPRINT",EDGE,{"derivedFrom":subQ35})])]}),makeQuery(id+"F10.opExtrude","SWEPT_FACE",FACE,{"disambiguationData":[OSD([sQuery(id+"F8.wireOp",EDGE,"E12.5.0")])]})])],"derivedFrom":makeQuery(id+"F3.boolean.opBoolean","COPY",EDGE,{"derivedFrom":makeQuery(id+"F3.opExtrude","CAP_EDGE",EDGE,{"disambiguationData":[OSD([subQ0])],"isStart":false})})});Q0=makeQuery(id+"F21.boolean.opBoolean","MERGE",EDGE,{"derivedFrom":[makeQuery(id+"F16.boolean.opBoolean","SPLIT",EDGE,{"disambiguationData":[TD([makeQuery(id+"F16.opExtrude","SWEPT_FACE",FACE,{"disambiguationData":[OSD([subQ17])]})])],"derivedFrom":subQ36}),makeQuery(id+"F16.boolean.opBoolean","SPLIT",EDGE,{"disambiguationData":[TD([makeQuery(id+"F16.opExtrude","SWEPT_FACE",FACE,{"disambiguationData":[OSD([subQ24])]})])],"derivedFrom":subQ36}),makeQuery(id+"F16.boolean.opBoolean","SPLIT",EDGE,{"disambiguationData":[TD([makeQuery(id+"F16.opExtrude","SWEPT_FACE",FACE,{"disambiguationData":[OSD([subQ20])]})])],"derivedFrom":subQ36}),makeQuery(id+"F16.boolean.opBoolean","SPLIT",EDGE,{"disambiguationData":[TD([makeQuery(id+"F16.opExtrude","SWEPT_FACE",FACE,{"disambiguationData":[OSD([subQ10])]})])],"derivedFrom":subQ36}),makeQuery(id+"F21.opExtrude","CAP_EDGE",EDGE,{"disambiguationData":[OSD([sQuery(id+"F20.wireOp",EDGE,"E26.4.0")])],"isStart":true}),makeQuery(id+"F21.opExtrude","CAP_EDGE",EDGE,{"disambiguationData":[OSD([sQuery(id+"F20.wireOp",EDGE,"E26.5.0")])],"isStart":true}),makeQuery(id+"F21.opExtrude","CAP_EDGE",EDGE,{"disambiguationData":[OSD([sQuery(id+"F20.wireOp",EDGE,"E26.6.0")])],"isStart":true}),makeQuery(id+"F21.opExtrude","CAP_EDGE",EDGE,{"disambiguationData":[OSD([sQuery(id+"F20.wireOp",EDGE,"E26.7.0")])],"isStart":true}),makeQuery(id+"F21.opExtrude","CAP_EDGE",EDGE,{"disambiguationData":[OSD([sQuery(id+"F20.wireOp",EDGE,"E26.8.0")])],"isStart":true})]});}
            var Q1;
            {var subQ0=sQuery(id+"F2.wireOp",EDGE,"E6");var subQ11=sQuery(id+"F15.wireOp",EDGE,"E20.1.3");var subQ15=sQuery(id+"F15.wireOp",EDGE,"E19.MirrorCS");var subQ17=sQuery(id+"F15.wireOp",EDGE,"E20.2.3");var subQ21=makeQuery(id+"F3.boolean.opBoolean","COPY",FACE,{"derivedFrom":makeQuery(id+"F3.opExtrude","CAP_FACE",FACE,{"disambiguationData":[OSD([subQ0])],"isStart":false})});var subQ23=makeQuery(id+"F3.boolean.opBoolean","COPY",FACE,{"derivedFrom":makeQuery(id+"F3.opExtrude","SWEPT_FACE",FACE,{"disambiguationData":[OSD([subQ0])]})});var subQ24=sQuery(id+"F15.wireOp",EDGE,"E20.3.3");var subQ35=sQuery(id+"F8.wireOp",EDGE,"E11");var subQ36=makeQuery(id+"F10.boolean.opBoolean","SPLIT",EDGE,{"disambiguationData":[TD([subQ23,subQ21,makeQuery(id+"F10.opExtrude","SWEPT_FACE",FACE,{"disambiguationData":[OSD([subQ35]),TDD([makeQuery(id+"F8.imprint","IMPRINT",EDGE,{"derivedFrom":subQ35})])]}),makeQuery(id+"F10.opExtrude","SWEPT_FACE",FACE,{"disambiguationData":[OSD([sQuery(id+"F8.wireOp",EDGE,"E12.5.0")])]})])],"derivedFrom":makeQuery(id+"F3.boolean.opBoolean","COPY",EDGE,{"derivedFrom":makeQuery(id+"F3.opExtrude","CAP_EDGE",EDGE,{"disambiguationData":[OSD([subQ0])],"isStart":false})})});Q1=makeQuery(id+"F21.boolean.opBoolean","MERGE",EDGE,{"derivedFrom":[makeQuery(id+"F16.boolean.opBoolean","SPLIT",EDGE,{"disambiguationData":[TD([makeQuery(id+"F16.opExtrude","SWEPT_FACE",FACE,{"disambiguationData":[OSD([subQ15])]})])],"derivedFrom":subQ36}),makeQuery(id+"F16.boolean.opBoolean","SPLIT",EDGE,{"disambiguationData":[TD([makeQuery(id+"F16.opExtrude","SWEPT_FACE",FACE,{"disambiguationData":[OSD([subQ11])]})])],"derivedFrom":subQ36}),makeQuery(id+"F16.boolean.opBoolean","SPLIT",EDGE,{"disambiguationData":[TD([makeQuery(id+"F16.opExtrude","SWEPT_FACE",FACE,{"disambiguationData":[OSD([subQ17])]})])],"derivedFrom":subQ36}),makeQuery(id+"F16.boolean.opBoolean","SPLIT",EDGE,{"disambiguationData":[TD([makeQuery(id+"F16.opExtrude","SWEPT_FACE",FACE,{"disambiguationData":[OSD([subQ24])]})])],"derivedFrom":subQ36}),makeQuery(id+"F21.opExtrude","CAP_EDGE",EDGE,{"disambiguationData":[OSD([sQuery(id+"F20.wireOp",EDGE,"E25")])],"isStart":true}),makeQuery(id+"F21.opExtrude","CAP_EDGE",EDGE,{"disambiguationData":[OSD([sQuery(id+"F20.wireOp",EDGE,"E26.1.0")])],"isStart":true}),makeQuery(id+"F21.opExtrude","CAP_EDGE",EDGE,{"disambiguationData":[OSD([sQuery(id+"F20.wireOp",EDGE,"E26.2.0")])],"isStart":true}),makeQuery(id+"F21.opExtrude","CAP_EDGE",EDGE,{"disambiguationData":[OSD([sQuery(id+"F20.wireOp",EDGE,"E26.3.0")])],"isStart":true}),makeQuery(id+"F21.opExtrude","CAP_EDGE",EDGE,{"disambiguationData":[OSD([sQuery(id+"F20.wireOp",EDGE,"E26.4.0")])],"isStart":true})]});}
            var Q2;
            {var subQ0=sQuery(id+"F2.wireOp",EDGE,"E6");var subQ7=sQuery(id+"F15.wireOp",EDGE,"E20.22.3");var subQ13=sQuery(id+"F15.wireOp",EDGE,"E17");var subQ17=makeQuery(id+"F3.boolean.opBoolean","COPY",FACE,{"derivedFrom":makeQuery(id+"F3.opExtrude","CAP_FACE",FACE,{"disambiguationData":[OSD([subQ0])],"isStart":false})});var subQ20=makeQuery(id+"F3.boolean.opBoolean","COPY",FACE,{"derivedFrom":makeQuery(id+"F3.opExtrude","SWEPT_FACE",FACE,{"disambiguationData":[OSD([subQ0])]})});var subQ25=sQuery(id+"F15.wireOp",EDGE,"E20.20.3");var subQ27=sQuery(id+"F15.wireOp",EDGE,"E20.21.3");var subQ35=sQuery(id+"F8.wireOp",EDGE,"E12.1.0");var subQ36=sQuery(id+"F8.wireOp",EDGE,"E11");var subQ37=makeQuery(id+"F10.boolean.opBoolean","SPLIT",EDGE,{"disambiguationData":[TD([subQ20,subQ17,makeQuery(id+"F10.opExtrude","SWEPT_FACE",FACE,{"disambiguationData":[OSD([subQ36]),TDD([makeQuery(id+"F8.imprint","IMPRINT",EDGE,{"derivedFrom":subQ36})])]}),makeQuery(id+"F10.opExtrude","SWEPT_FACE",FACE,{"disambiguationData":[OSD([subQ35]),TDD([makeQuery(id+"F8.imprint","IMPRINT",EDGE,{"derivedFrom":subQ35})])]})])],"derivedFrom":makeQuery(id+"F3.boolean.opBoolean","COPY",EDGE,{"derivedFrom":makeQuery(id+"F3.opExtrude","CAP_EDGE",EDGE,{"disambiguationData":[OSD([subQ0])],"isStart":false})})});Q2=makeQuery(id+"F21.boolean.opBoolean","MERGE",EDGE,{"derivedFrom":[makeQuery(id+"F16.boolean.opBoolean","SPLIT",EDGE,{"disambiguationData":[TD([makeQuery(id+"F16.opExtrude","SWEPT_FACE",FACE,{"disambiguationData":[OSD([subQ13])]})])],"derivedFrom":subQ37}),makeQuery(id+"F16.boolean.opBoolean","SPLIT",EDGE,{"disambiguationData":[TD([makeQuery(id+"F16.opExtrude","SWEPT_FACE",FACE,{"disambiguationData":[OSD([subQ25])]})])],"derivedFrom":subQ37}),makeQuery(id+"F16.boolean.opBoolean","SPLIT",EDGE,{"disambiguationData":[TD([makeQuery(id+"F16.opExtrude","SWEPT_FACE",FACE,{"disambiguationData":[OSD([subQ27])]})])],"derivedFrom":subQ37}),makeQuery(id+"F16.boolean.opBoolean","SPLIT",EDGE,{"disambiguationData":[TD([makeQuery(id+"F16.opExtrude","SWEPT_FACE",FACE,{"disambiguationData":[OSD([subQ7])]})])],"derivedFrom":subQ37}),makeQuery(id+"F21.opExtrude","CAP_EDGE",EDGE,{"disambiguationData":[OSD([sQuery(id+"F20.wireOp",EDGE,"E25")])],"isStart":true}),makeQuery(id+"F21.opExtrude","CAP_EDGE",EDGE,{"disambiguationData":[OSD([sQuery(id+"F20.wireOp",EDGE,"E26.20.0")])],"isStart":true}),makeQuery(id+"F21.opExtrude","CAP_EDGE",EDGE,{"disambiguationData":[OSD([sQuery(id+"F20.wireOp",EDGE,"E26.21.0")])],"isStart":true}),makeQuery(id+"F21.opExtrude","CAP_EDGE",EDGE,{"disambiguationData":[OSD([sQuery(id+"F20.wireOp",EDGE,"E26.22.0")])],"isStart":true}),makeQuery(id+"F21.opExtrude","CAP_EDGE",EDGE,{"disambiguationData":[OSD([sQuery(id+"F20.wireOp",EDGE,"E26.23.0")])],"isStart":true})]});}
            var Q3;
            {var subQ0=sQuery(id+"F15.wireOp",EDGE,"E20.18.3");var subQ2=sQuery(id+"F2.wireOp",EDGE,"E6");var subQ4=sQuery(id+"F15.wireOp",EDGE,"E20.17.3");var subQ7=sQuery(id+"F15.wireOp",EDGE,"E20.16.3");var subQ20=sQuery(id+"F15.wireOp",EDGE,"E20.19.3");var subQ21=makeQuery(id+"F3.boolean.opBoolean","COPY",FACE,{"derivedFrom":makeQuery(id+"F3.opExtrude","CAP_FACE",FACE,{"disambiguationData":[OSD([subQ2])],"isStart":false})});var subQ25=makeQuery(id+"F3.boolean.opBoolean","COPY",FACE,{"derivedFrom":makeQuery(id+"F3.opExtrude","SWEPT_FACE",FACE,{"disambiguationData":[OSD([subQ2])]})});var subQ35=sQuery(id+"F8.wireOp",EDGE,"E12.1.0");var subQ36=sQuery(id+"F8.wireOp",EDGE,"E12.2.0");var subQ37=makeQuery(id+"F10.boolean.opBoolean","SPLIT",EDGE,{"disambiguationData":[TD([subQ25,subQ21,makeQuery(id+"F10.opExtrude","SWEPT_FACE",FACE,{"disambiguationData":[OSD([subQ35]),TDD([makeQuery(id+"F8.imprint","IMPRINT",EDGE,{"derivedFrom":subQ35})])]}),makeQuery(id+"F10.opExtrude","SWEPT_FACE",FACE,{"disambiguationData":[OSD([subQ36]),TDD([makeQuery(id+"F8.imprint","IMPRINT",EDGE,{"derivedFrom":subQ36})])]})])],"derivedFrom":makeQuery(id+"F3.boolean.opBoolean","COPY",EDGE,{"derivedFrom":makeQuery(id+"F3.opExtrude","CAP_EDGE",EDGE,{"disambiguationData":[OSD([subQ2])],"isStart":false})})});Q3=makeQuery(id+"F21.boolean.opBoolean","MERGE",EDGE,{"derivedFrom":[makeQuery(id+"F16.boolean.opBoolean","SPLIT",EDGE,{"disambiguationData":[TD([makeQuery(id+"F16.opExtrude","SWEPT_FACE",FACE,{"disambiguationData":[OSD([subQ7])]})])],"derivedFrom":subQ37}),makeQuery(id+"F16.boolean.opBoolean","SPLIT",EDGE,{"disambiguationData":[TD([makeQuery(id+"F16.opExtrude","SWEPT_FACE",FACE,{"disambiguationData":[OSD([subQ4])]})])],"derivedFrom":subQ37}),makeQuery(id+"F16.boolean.opBoolean","SPLIT",EDGE,{"disambiguationData":[TD([makeQuery(id+"F16.opExtrude","SWEPT_FACE",FACE,{"disambiguationData":[OSD([subQ0])]})])],"derivedFrom":subQ37}),makeQuery(id+"F16.boolean.opBoolean","SPLIT",EDGE,{"disambiguationData":[TD([makeQuery(id+"F16.opExtrude","SWEPT_FACE",FACE,{"disambiguationData":[OSD([subQ20])]})])],"derivedFrom":subQ37}),makeQuery(id+"F21.opExtrude","CAP_EDGE",EDGE,{"disambiguationData":[OSD([sQuery(id+"F20.wireOp",EDGE,"E26.16.0")])],"isStart":true}),makeQuery(id+"F21.opExtrude","CAP_EDGE",EDGE,{"disambiguationData":[OSD([sQuery(id+"F20.wireOp",EDGE,"E26.17.0")])],"isStart":true}),makeQuery(id+"F21.opExtrude","CAP_EDGE",EDGE,{"disambiguationData":[OSD([sQuery(id+"F20.wireOp",EDGE,"E26.18.0")])],"isStart":true}),makeQuery(id+"F21.opExtrude","CAP_EDGE",EDGE,{"disambiguationData":[OSD([sQuery(id+"F20.wireOp",EDGE,"E26.19.0")])],"isStart":true}),makeQuery(id+"F21.opExtrude","CAP_EDGE",EDGE,{"disambiguationData":[OSD([sQuery(id+"F20.wireOp",EDGE,"E26.20.0")])],"isStart":true})]});}
            var Q4;
            {var subQ0=sQuery(id+"F2.wireOp",EDGE,"E6");var subQ4=sQuery(id+"F15.wireOp",EDGE,"E20.15.3");var subQ8=sQuery(id+"F15.wireOp",EDGE,"E20.14.3");var subQ11=sQuery(id+"F15.wireOp",EDGE,"E20.13.3");var subQ14=sQuery(id+"F15.wireOp",EDGE,"E20.12.3");var subQ16=makeQuery(id+"F3.boolean.opBoolean","COPY",FACE,{"derivedFrom":makeQuery(id+"F3.opExtrude","SWEPT_FACE",FACE,{"disambiguationData":[OSD([subQ0])]})});var subQ24=makeQuery(id+"F3.boolean.opBoolean","COPY",FACE,{"derivedFrom":makeQuery(id+"F3.opExtrude","CAP_FACE",FACE,{"disambiguationData":[OSD([subQ0])],"isStart":false})});var subQ35=sQuery(id+"F8.wireOp",EDGE,"E12.2.0");var subQ36=sQuery(id+"F8.wireOp",EDGE,"E12.3.0");var subQ37=makeQuery(id+"F10.boolean.opBoolean","SPLIT",EDGE,{"disambiguationData":[TD([subQ16,subQ24,makeQuery(id+"F10.opExtrude","SWEPT_FACE",FACE,{"disambiguationData":[OSD([subQ35]),TDD([makeQuery(id+"F8.imprint","IMPRINT",EDGE,{"derivedFrom":subQ35})])]}),makeQuery(id+"F10.opExtrude","SWEPT_FACE",FACE,{"disambiguationData":[OSD([subQ36]),TDD([makeQuery(id+"F8.imprint","IMPRINT",EDGE,{"derivedFrom":subQ36})])]})])],"derivedFrom":makeQuery(id+"F3.boolean.opBoolean","COPY",EDGE,{"derivedFrom":makeQuery(id+"F3.opExtrude","CAP_EDGE",EDGE,{"disambiguationData":[OSD([subQ0])],"isStart":false})})});Q4=makeQuery(id+"F21.boolean.opBoolean","MERGE",EDGE,{"derivedFrom":[makeQuery(id+"F16.boolean.opBoolean","SPLIT",EDGE,{"disambiguationData":[TD([makeQuery(id+"F16.opExtrude","SWEPT_FACE",FACE,{"disambiguationData":[OSD([subQ14])]})])],"derivedFrom":subQ37}),makeQuery(id+"F16.boolean.opBoolean","SPLIT",EDGE,{"disambiguationData":[TD([makeQuery(id+"F16.opExtrude","SWEPT_FACE",FACE,{"disambiguationData":[OSD([subQ11])]})])],"derivedFrom":subQ37}),makeQuery(id+"F16.boolean.opBoolean","SPLIT",EDGE,{"disambiguationData":[TD([makeQuery(id+"F16.opExtrude","SWEPT_FACE",FACE,{"disambiguationData":[OSD([subQ8])]})])],"derivedFrom":subQ37}),makeQuery(id+"F16.boolean.opBoolean","SPLIT",EDGE,{"disambiguationData":[TD([makeQuery(id+"F16.opExtrude","SWEPT_FACE",FACE,{"disambiguationData":[OSD([subQ4])]})])],"derivedFrom":subQ37}),makeQuery(id+"F21.opExtrude","CAP_EDGE",EDGE,{"disambiguationData":[OSD([sQuery(id+"F20.wireOp",EDGE,"E26.12.0")])],"isStart":true}),makeQuery(id+"F21.opExtrude","CAP_EDGE",EDGE,{"disambiguationData":[OSD([sQuery(id+"F20.wireOp",EDGE,"E26.13.0")])],"isStart":true}),makeQuery(id+"F21.opExtrude","CAP_EDGE",EDGE,{"disambiguationData":[OSD([sQuery(id+"F20.wireOp",EDGE,"E26.14.0")])],"isStart":true}),makeQuery(id+"F21.opExtrude","CAP_EDGE",EDGE,{"disambiguationData":[OSD([sQuery(id+"F20.wireOp",EDGE,"E26.15.0")])],"isStart":true}),makeQuery(id+"F21.opExtrude","CAP_EDGE",EDGE,{"disambiguationData":[OSD([sQuery(id+"F20.wireOp",EDGE,"E26.16.0")])],"isStart":true})]});}
            var Q5;
            {var subQ0=sQuery(id+"F2.wireOp",EDGE,"E6");var subQ8=sQuery(id+"F15.wireOp",EDGE,"E20.11.3");var subQ12=sQuery(id+"F15.wireOp",EDGE,"E20.8.3");var subQ15=sQuery(id+"F15.wireOp",EDGE,"E20.9.3");var subQ19=sQuery(id+"F15.wireOp",EDGE,"E20.10.3");var subQ22=makeQuery(id+"F3.boolean.opBoolean","COPY",FACE,{"derivedFrom":makeQuery(id+"F3.opExtrude","CAP_FACE",FACE,{"disambiguationData":[OSD([subQ0])],"isStart":false})});var subQ24=makeQuery(id+"F3.boolean.opBoolean","COPY",FACE,{"derivedFrom":makeQuery(id+"F3.opExtrude","SWEPT_FACE",FACE,{"disambiguationData":[OSD([subQ0])]})});var subQ35=sQuery(id+"F8.wireOp",EDGE,"E12.4.0");var subQ36=sQuery(id+"F8.wireOp",EDGE,"E12.3.0");var subQ37=makeQuery(id+"F10.boolean.opBoolean","SPLIT",EDGE,{"disambiguationData":[TD([subQ24,subQ22,makeQuery(id+"F10.opExtrude","SWEPT_FACE",FACE,{"disambiguationData":[OSD([subQ36]),TDD([makeQuery(id+"F8.imprint","IMPRINT",EDGE,{"derivedFrom":subQ36})])]}),makeQuery(id+"F10.opExtrude","SWEPT_FACE",FACE,{"disambiguationData":[OSD([subQ35]),TDD([makeQuery(id+"F8.imprint","IMPRINT",EDGE,{"derivedFrom":subQ35})])]})])],"derivedFrom":makeQuery(id+"F3.boolean.opBoolean","COPY",EDGE,{"derivedFrom":makeQuery(id+"F3.opExtrude","CAP_EDGE",EDGE,{"disambiguationData":[OSD([subQ0])],"isStart":false})})});Q5=makeQuery(id+"F21.boolean.opBoolean","MERGE",EDGE,{"derivedFrom":[makeQuery(id+"F16.boolean.opBoolean","SPLIT",EDGE,{"disambiguationData":[TD([makeQuery(id+"F16.opExtrude","SWEPT_FACE",FACE,{"disambiguationData":[OSD([subQ12])]})])],"derivedFrom":subQ37}),makeQuery(id+"F16.boolean.opBoolean","SPLIT",EDGE,{"disambiguationData":[TD([makeQuery(id+"F16.opExtrude","SWEPT_FACE",FACE,{"disambiguationData":[OSD([subQ15])]})])],"derivedFrom":subQ37}),makeQuery(id+"F16.boolean.opBoolean","SPLIT",EDGE,{"disambiguationData":[TD([makeQuery(id+"F16.opExtrude","SWEPT_FACE",FACE,{"disambiguationData":[OSD([subQ19])]})])],"derivedFrom":subQ37}),makeQuery(id+"F16.boolean.opBoolean","SPLIT",EDGE,{"disambiguationData":[TD([makeQuery(id+"F16.opExtrude","SWEPT_FACE",FACE,{"disambiguationData":[OSD([subQ8])]})])],"derivedFrom":subQ37}),makeQuery(id+"F21.opExtrude","CAP_EDGE",EDGE,{"disambiguationData":[OSD([sQuery(id+"F20.wireOp",EDGE,"E26.8.0")])],"isStart":true}),makeQuery(id+"F21.opExtrude","CAP_EDGE",EDGE,{"disambiguationData":[OSD([sQuery(id+"F20.wireOp",EDGE,"E26.9.0")])],"isStart":true}),makeQuery(id+"F21.opExtrude","CAP_EDGE",EDGE,{"disambiguationData":[OSD([sQuery(id+"F20.wireOp",EDGE,"E26.10.0")])],"isStart":true}),makeQuery(id+"F21.opExtrude","CAP_EDGE",EDGE,{"disambiguationData":[OSD([sQuery(id+"F20.wireOp",EDGE,"E26.11.0")])],"isStart":true}),makeQuery(id+"F21.opExtrude","CAP_EDGE",EDGE,{"disambiguationData":[OSD([sQuery(id+"F20.wireOp",EDGE,"E26.12.0")])],"isStart":true})]});}
            fillet(context, id + "F24", {"entities" : qUnion([Q0, Q1, Q2, Q3, Q4, Q5]), "radius" : 5.08 * mm, "allowEdgeOverflow" : false});
        }
    });
